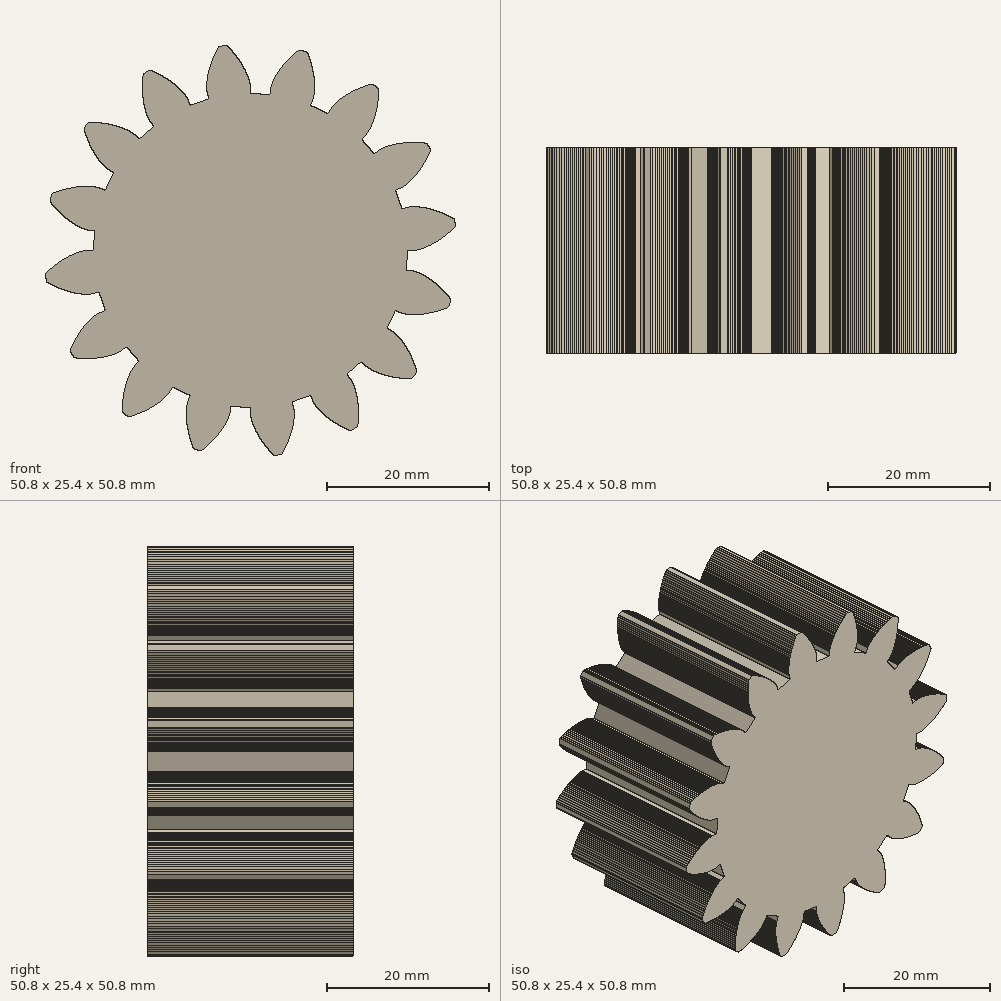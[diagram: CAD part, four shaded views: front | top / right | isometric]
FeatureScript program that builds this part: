
annotation { "Feature Type Name" : "Feature", "Feature Type Description" : "" }
export const myFeature = defineFeature(function(context is Context, id is Id, definition is map)
    precondition{}
    {
        {
            var Q0;
            Q0=qCreatedBy(makeId("Front.planeOp"),FACE);
            var sketch = newSketch(context, id + "F0", { "sketchPlane" : qUnion([Q0])});
            skLineSegment(sketch, "E0", {"start": v(19.47, 0) * mm, "end": v(20.26, 0) * mm});
            skLineSegment(sketch, "E1", {"start": v(20.26, 0) * mm, "end": v(20.27, 0) * mm});
            skLineSegment(sketch, "E2", {"start": v(20.27, 0) * mm, "end": v(20.3, 0) * mm});
            skLineSegment(sketch, "E3", {"start": v(20.3, 0) * mm, "end": v(20.33, 0) * mm});
            skLineSegment(sketch, "E4", {"start": v(20.33, 0) * mm, "end": v(20.37, 0) * mm});
            skLineSegment(sketch, "E5", {"start": v(20.37, 0) * mm, "end": v(20.42, 0.01) * mm});
            skLineSegment(sketch, "E6", {"start": v(20.42, 0.01) * mm, "end": v(20.48, 0.02) * mm});
            skLineSegment(sketch, "E7", {"start": v(20.48, 0.02) * mm, "end": v(20.55, 0.03) * mm});
            skLineSegment(sketch, "E8", {"start": v(20.55, 0.03) * mm, "end": v(20.63, 0.05) * mm});
            skLineSegment(sketch, "E9", {"start": v(20.63, 0.05) * mm, "end": v(20.72, 0.07) * mm});
            skLineSegment(sketch, "E10", {"start": v(20.72, 0.07) * mm, "end": v(20.81, 0.09) * mm});
            skLineSegment(sketch, "E11", {"start": v(20.81, 0.09) * mm, "end": v(20.92, 0.11) * mm});
            skLineSegment(sketch, "E12", {"start": v(20.92, 0.11) * mm, "end": v(21.03, 0.15) * mm});
            skLineSegment(sketch, "E13", {"start": v(21.03, 0.15) * mm, "end": v(21.15, 0.18) * mm});
            skLineSegment(sketch, "E14", {"start": v(21.15, 0.18) * mm, "end": v(21.29, 0.22) * mm});
            skLineSegment(sketch, "E15", {"start": v(21.29, 0.22) * mm, "end": v(21.43, 0.27) * mm});
            skLineSegment(sketch, "E16", {"start": v(21.43, 0.27) * mm, "end": v(21.57, 0.33) * mm});
            skLineSegment(sketch, "E17", {"start": v(21.57, 0.33) * mm, "end": v(21.73, 0.39) * mm});
            skLineSegment(sketch, "E18", {"start": v(21.73, 0.39) * mm, "end": v(21.9, 0.46) * mm});
            skLineSegment(sketch, "E19", {"start": v(21.9, 0.46) * mm, "end": v(22.06, 0.53) * mm});
            skLineSegment(sketch, "E20", {"start": v(22.06, 0.53) * mm, "end": v(22.24, 0.62) * mm});
            skLineSegment(sketch, "E21", {"start": v(22.24, 0.62) * mm, "end": v(22.42, 0.71) * mm});
            skLineSegment(sketch, "E22", {"start": v(22.42, 0.71) * mm, "end": v(22.61, 0.81) * mm});
            skLineSegment(sketch, "E23", {"start": v(22.61, 0.81) * mm, "end": v(22.8, 0.92) * mm});
            skLineSegment(sketch, "E24", {"start": v(22.8, 0.92) * mm, "end": v(23, 1.04) * mm});
            skLineSegment(sketch, "E25", {"start": v(23, 1.04) * mm, "end": v(23.22, 1.17) * mm});
            skLineSegment(sketch, "E26", {"start": v(23.22, 1.17) * mm, "end": v(23.43, 1.3) * mm});
            skLineSegment(sketch, "E27", {"start": v(23.43, 1.3) * mm, "end": v(23.65, 1.45) * mm});
            skLineSegment(sketch, "E28", {"start": v(23.65, 1.45) * mm, "end": v(23.87, 1.6) * mm});
            skLineSegment(sketch, "E29", {"start": v(23.87, 1.6) * mm, "end": v(24.1, 1.78) * mm});
            skLineSegment(sketch, "E30", {"start": v(24.1, 1.78) * mm, "end": v(24.33, 1.96) * mm});
            skLineSegment(sketch, "E31", {"start": v(24.33, 1.96) * mm, "end": v(24.56, 2.15) * mm});
            skLineSegment(sketch, "E32", {"start": v(24.56, 2.15) * mm, "end": v(24.8, 2.35) * mm});
            skLineSegment(sketch, "E33", {"start": v(24.8, 2.35) * mm, "end": v(25.04, 2.56) * mm});
            skLineSegment(sketch, "E34", {"start": v(25.04, 2.56) * mm, "end": v(25.28, 2.79) * mm});
            skLineSegment(sketch, "E35", {"start": v(25.28, 2.79) * mm, "end": v(25.4, 3.01) * mm});
            skLineSegment(sketch, "E36", {"start": v(25.4, 3.01) * mm, "end": v(25.3, 3.82) * mm});
            skLineSegment(sketch, "E37", {"start": v(25.3, 3.82) * mm, "end": v(25.12, 4) * mm});
            skLineSegment(sketch, "E38", {"start": v(25.12, 4) * mm, "end": v(24.82, 4.16) * mm});
            skLineSegment(sketch, "E39", {"start": v(24.82, 4.16) * mm, "end": v(24.54, 4.3) * mm});
            skLineSegment(sketch, "E40", {"start": v(24.54, 4.3) * mm, "end": v(24.25, 4.43) * mm});
            skLineSegment(sketch, "E41", {"start": v(24.25, 4.43) * mm, "end": v(23.98, 4.55) * mm});
            skLineSegment(sketch, "E42", {"start": v(23.98, 4.55) * mm, "end": v(23.7, 4.67) * mm});
            skLineSegment(sketch, "E43", {"start": v(23.7, 4.67) * mm, "end": v(23.44, 4.77) * mm});
            skLineSegment(sketch, "E44", {"start": v(23.44, 4.77) * mm, "end": v(23.19, 4.86) * mm});
            skLineSegment(sketch, "E45", {"start": v(23.19, 4.86) * mm, "end": v(22.94, 4.95) * mm});
            skLineSegment(sketch, "E46", {"start": v(22.94, 4.95) * mm, "end": v(22.7, 5.02) * mm});
            skLineSegment(sketch, "E47", {"start": v(22.7, 5.02) * mm, "end": v(22.46, 5.1) * mm});
            skLineSegment(sketch, "E48", {"start": v(22.46, 5.1) * mm, "end": v(22.24, 5.15) * mm});
            skLineSegment(sketch, "E49", {"start": v(22.24, 5.15) * mm, "end": v(22.02, 5.2) * mm});
            skLineSegment(sketch, "E50", {"start": v(22.02, 5.2) * mm, "end": v(21.8, 5.25) * mm});
            skLineSegment(sketch, "E51", {"start": v(21.8, 5.25) * mm, "end": v(21.6, 5.3) * mm});
            skLineSegment(sketch, "E52", {"start": v(21.6, 5.3) * mm, "end": v(21.41, 5.33) * mm});
            skLineSegment(sketch, "E53", {"start": v(21.41, 5.33) * mm, "end": v(21.23, 5.36) * mm});
            skLineSegment(sketch, "E54", {"start": v(21.23, 5.36) * mm, "end": v(21.06, 5.38) * mm});
            skLineSegment(sketch, "E55", {"start": v(21.06, 5.38) * mm, "end": v(20.89, 5.4) * mm});
            skLineSegment(sketch, "E56", {"start": v(20.89, 5.4) * mm, "end": v(20.73, 5.41) * mm});
            skLineSegment(sketch, "E57", {"start": v(20.73, 5.41) * mm, "end": v(20.59, 5.42) * mm});
            skLineSegment(sketch, "E58", {"start": v(20.59, 5.42) * mm, "end": v(20.45, 5.43) * mm});
            skLineSegment(sketch, "E59", {"start": v(20.45, 5.43) * mm, "end": v(20.32, 5.43) * mm});
            skLineSegment(sketch, "E60", {"start": v(20.32, 5.43) * mm, "end": v(20.2, 5.43) * mm});
            skLineSegment(sketch, "E61", {"start": v(20.2, 5.43) * mm, "end": v(20.1, 5.43) * mm});
            skLineSegment(sketch, "E62", {"start": v(20.1, 5.43) * mm, "end": v(20, 5.42) * mm});
            skLineSegment(sketch, "E63", {"start": v(20, 5.42) * mm, "end": v(19.9, 5.42) * mm});
            skLineSegment(sketch, "E64", {"start": v(19.9, 5.42) * mm, "end": v(19.82, 5.4) * mm});
            skLineSegment(sketch, "E65", {"start": v(19.82, 5.4) * mm, "end": v(19.75, 5.4) * mm});
            skLineSegment(sketch, "E66", {"start": v(19.75, 5.4) * mm, "end": v(19.7, 5.4) * mm});
            skLineSegment(sketch, "E67", {"start": v(19.7, 5.4) * mm, "end": v(19.64, 5.39) * mm});
            skLineSegment(sketch, "E68", {"start": v(19.64, 5.39) * mm, "end": v(19.6, 5.38) * mm});
            skLineSegment(sketch, "E69", {"start": v(19.6, 5.38) * mm, "end": v(19.57, 5.37) * mm});
            skLineSegment(sketch, "E70", {"start": v(19.57, 5.37) * mm, "end": v(19.55, 5.37) * mm});
            skLineSegment(sketch, "E71", {"start": v(19.55, 5.37) * mm, "end": v(19.54, 5.37) * mm});
            skLineSegment(sketch, "E72", {"start": v(19.54, 5.37) * mm, "end": v(18.77, 5.16) * mm});
            skLineSegment(sketch, "E73", {"start": v(18.77, 5.16) * mm, "end": v(17.99, 7.45) * mm});
            skLineSegment(sketch, "E74", {"start": v(17.99, 7.45) * mm, "end": v(18.72, 7.75) * mm});
            skLineSegment(sketch, "E75", {"start": v(18.72, 7.75) * mm, "end": v(18.73, 7.76) * mm});
            skLineSegment(sketch, "E76", {"start": v(18.73, 7.76) * mm, "end": v(18.75, 7.77) * mm});
            skLineSegment(sketch, "E77", {"start": v(18.75, 7.77) * mm, "end": v(18.78, 7.78) * mm});
            skLineSegment(sketch, "E78", {"start": v(18.78, 7.78) * mm, "end": v(18.82, 7.8) * mm});
            skLineSegment(sketch, "E79", {"start": v(18.82, 7.8) * mm, "end": v(18.86, 7.83) * mm});
            skLineSegment(sketch, "E80", {"start": v(18.86, 7.83) * mm, "end": v(18.91, 7.86) * mm});
            skLineSegment(sketch, "E81", {"start": v(18.91, 7.86) * mm, "end": v(18.97, 7.9) * mm});
            skLineSegment(sketch, "E82", {"start": v(18.97, 7.9) * mm, "end": v(19.04, 7.94) * mm});
            skLineSegment(sketch, "E83", {"start": v(19.04, 7.94) * mm, "end": v(19.11, 7.99) * mm});
            skLineSegment(sketch, "E84", {"start": v(19.11, 7.99) * mm, "end": v(19.2, 8.05) * mm});
            skLineSegment(sketch, "E85", {"start": v(19.2, 8.05) * mm, "end": v(19.28, 8.11) * mm});
            skLineSegment(sketch, "E86", {"start": v(19.28, 8.11) * mm, "end": v(19.38, 8.18) * mm});
            skLineSegment(sketch, "E87", {"start": v(19.38, 8.18) * mm, "end": v(19.47, 8.26) * mm});
            skLineSegment(sketch, "E88", {"start": v(19.47, 8.26) * mm, "end": v(19.58, 8.35) * mm});
            skLineSegment(sketch, "E89", {"start": v(19.58, 8.35) * mm, "end": v(19.7, 8.45) * mm});
            skLineSegment(sketch, "E90", {"start": v(19.7, 8.45) * mm, "end": v(19.8, 8.56) * mm});
            skLineSegment(sketch, "E91", {"start": v(19.8, 8.56) * mm, "end": v(19.93, 8.68) * mm});
            skLineSegment(sketch, "E92", {"start": v(19.93, 8.68) * mm, "end": v(20.05, 8.8) * mm});
            skLineSegment(sketch, "E93", {"start": v(20.05, 8.8) * mm, "end": v(20.18, 8.94) * mm});
            skLineSegment(sketch, "E94", {"start": v(20.18, 8.94) * mm, "end": v(20.3, 9.08) * mm});
            skLineSegment(sketch, "E95", {"start": v(20.3, 9.08) * mm, "end": v(20.44, 9.24) * mm});
            skLineSegment(sketch, "E96", {"start": v(20.44, 9.24) * mm, "end": v(20.58, 9.4) * mm});
            skLineSegment(sketch, "E97", {"start": v(20.58, 9.4) * mm, "end": v(20.72, 9.58) * mm});
            skLineSegment(sketch, "E98", {"start": v(20.72, 9.58) * mm, "end": v(20.86, 9.76) * mm});
            skLineSegment(sketch, "E99", {"start": v(20.86, 9.76) * mm, "end": v(21, 9.96) * mm});
            skLineSegment(sketch, "E100", {"start": v(21, 9.96) * mm, "end": v(21.15, 10.17) * mm});
            skLineSegment(sketch, "E101", {"start": v(21.15, 10.17) * mm, "end": v(21.3, 10.4) * mm});
            skLineSegment(sketch, "E102", {"start": v(21.3, 10.4) * mm, "end": v(21.44, 10.62) * mm});
            skLineSegment(sketch, "E103", {"start": v(21.44, 10.62) * mm, "end": v(21.58, 10.86) * mm});
            skLineSegment(sketch, "E104", {"start": v(21.58, 10.86) * mm, "end": v(21.73, 11.12) * mm});
            skLineSegment(sketch, "E105", {"start": v(21.73, 11.12) * mm, "end": v(21.87, 11.38) * mm});
            skLineSegment(sketch, "E106", {"start": v(21.87, 11.38) * mm, "end": v(22.01, 11.66) * mm});
            skLineSegment(sketch, "E107", {"start": v(22.01, 11.66) * mm, "end": v(22.15, 11.95) * mm});
            skLineSegment(sketch, "E108", {"start": v(22.15, 11.95) * mm, "end": v(22.29, 12.25) * mm});
            skLineSegment(sketch, "E109", {"start": v(22.29, 12.25) * mm, "end": v(22.31, 12.5) * mm});
            skLineSegment(sketch, "E110", {"start": v(22.31, 12.5) * mm, "end": v(21.9, 13.21) * mm});
            skLineSegment(sketch, "E111", {"start": v(21.9, 13.21) * mm, "end": v(21.67, 13.31) * mm});
            skLineSegment(sketch, "E112", {"start": v(21.67, 13.31) * mm, "end": v(21.34, 13.34) * mm});
            skLineSegment(sketch, "E113", {"start": v(21.34, 13.34) * mm, "end": v(21.02, 13.36) * mm});
            skLineSegment(sketch, "E114", {"start": v(21.02, 13.36) * mm, "end": v(20.71, 13.38) * mm});
            skLineSegment(sketch, "E115", {"start": v(20.71, 13.38) * mm, "end": v(20.4, 13.38) * mm});
            skLineSegment(sketch, "E116", {"start": v(20.4, 13.38) * mm, "end": v(20.12, 13.38) * mm});
            skLineSegment(sketch, "E117", {"start": v(20.12, 13.38) * mm, "end": v(19.83, 13.38) * mm});
            skLineSegment(sketch, "E118", {"start": v(19.83, 13.38) * mm, "end": v(19.56, 13.37) * mm});
            skLineSegment(sketch, "E119", {"start": v(19.56, 13.37) * mm, "end": v(19.3, 13.35) * mm});
            skLineSegment(sketch, "E120", {"start": v(19.3, 13.35) * mm, "end": v(19.05, 13.33) * mm});
            skLineSegment(sketch, "E121", {"start": v(19.05, 13.33) * mm, "end": v(18.8, 13.3) * mm});
            skLineSegment(sketch, "E122", {"start": v(18.8, 13.3) * mm, "end": v(18.57, 13.27) * mm});
            skLineSegment(sketch, "E123", {"start": v(18.57, 13.27) * mm, "end": v(18.35, 13.24) * mm});
            skLineSegment(sketch, "E124", {"start": v(18.35, 13.24) * mm, "end": v(18.14, 13.2) * mm});
            skLineSegment(sketch, "E125", {"start": v(18.14, 13.2) * mm, "end": v(17.94, 13.16) * mm});
            skLineSegment(sketch, "E126", {"start": v(17.94, 13.16) * mm, "end": v(17.75, 13.12) * mm});
            skLineSegment(sketch, "E127", {"start": v(17.75, 13.12) * mm, "end": v(17.56, 13.07) * mm});
            skLineSegment(sketch, "E128", {"start": v(17.56, 13.07) * mm, "end": v(17.4, 13.03) * mm});
            skLineSegment(sketch, "E129", {"start": v(17.4, 13.03) * mm, "end": v(17.23, 12.98) * mm});
            skLineSegment(sketch, "E130", {"start": v(17.23, 12.98) * mm, "end": v(17.08, 12.93) * mm});
            skLineSegment(sketch, "E131", {"start": v(17.08, 12.93) * mm, "end": v(16.94, 12.89) * mm});
            skLineSegment(sketch, "E132", {"start": v(16.94, 12.89) * mm, "end": v(16.82, 12.84) * mm});
            skLineSegment(sketch, "E133", {"start": v(16.82, 12.84) * mm, "end": v(16.7, 12.8) * mm});
            skLineSegment(sketch, "E134", {"start": v(16.7, 12.8) * mm, "end": v(16.59, 12.75) * mm});
            skLineSegment(sketch, "E135", {"start": v(16.59, 12.75) * mm, "end": v(16.49, 12.7) * mm});
            skLineSegment(sketch, "E136", {"start": v(16.49, 12.7) * mm, "end": v(16.4, 12.66) * mm});
            skLineSegment(sketch, "E137", {"start": v(16.4, 12.66) * mm, "end": v(16.32, 12.62) * mm});
            skLineSegment(sketch, "E138", {"start": v(16.32, 12.62) * mm, "end": v(16.24, 12.58) * mm});
            skLineSegment(sketch, "E139", {"start": v(16.24, 12.58) * mm, "end": v(16.18, 12.55) * mm});
            skLineSegment(sketch, "E140", {"start": v(16.18, 12.55) * mm, "end": v(16.13, 12.52) * mm});
            skLineSegment(sketch, "E141", {"start": v(16.13, 12.52) * mm, "end": v(16.09, 12.5) * mm});
            skLineSegment(sketch, "E142", {"start": v(16.09, 12.5) * mm, "end": v(16.05, 12.47) * mm});
            skLineSegment(sketch, "E143", {"start": v(16.05, 12.47) * mm, "end": v(16.03, 12.45) * mm});
            skLineSegment(sketch, "E144", {"start": v(16.03, 12.45) * mm, "end": v(16, 12.44) * mm});
            skLineSegment(sketch, "E145", {"start": v(16, 12.44) * mm, "end": v(16, 12.43) * mm});
            skLineSegment(sketch, "E146", {"start": v(16, 12.43) * mm, "end": v(15.37, 11.95) * mm});
            skLineSegment(sketch, "E147", {"start": v(15.37, 11.95) * mm, "end": v(13.77, 13.77) * mm});
            skLineSegment(sketch, "E148", {"start": v(13.77, 13.77) * mm, "end": v(14.33, 14.33) * mm});
            skLineSegment(sketch, "E149", {"start": v(14.33, 14.33) * mm, "end": v(14.34, 14.34) * mm});
            skLineSegment(sketch, "E150", {"start": v(14.34, 14.34) * mm, "end": v(14.35, 14.35) * mm});
            skLineSegment(sketch, "E151", {"start": v(14.35, 14.35) * mm, "end": v(14.37, 14.38) * mm});
            skLineSegment(sketch, "E152", {"start": v(14.37, 14.38) * mm, "end": v(14.4, 14.4) * mm});
            skLineSegment(sketch, "E153", {"start": v(14.4, 14.4) * mm, "end": v(14.43, 14.45) * mm});
            skLineSegment(sketch, "E154", {"start": v(14.43, 14.45) * mm, "end": v(14.47, 14.5) * mm});
            skLineSegment(sketch, "E155", {"start": v(14.47, 14.5) * mm, "end": v(14.5, 14.55) * mm});
            skLineSegment(sketch, "E156", {"start": v(14.5, 14.55) * mm, "end": v(14.55, 14.62) * mm});
            skLineSegment(sketch, "E157", {"start": v(14.55, 14.62) * mm, "end": v(14.6, 14.7) * mm});
            skLineSegment(sketch, "E158", {"start": v(14.6, 14.7) * mm, "end": v(14.65, 14.78) * mm});
            skLineSegment(sketch, "E159", {"start": v(14.65, 14.78) * mm, "end": v(14.71, 14.87) * mm});
            skLineSegment(sketch, "E160", {"start": v(14.71, 14.87) * mm, "end": v(14.77, 14.98) * mm});
            skLineSegment(sketch, "E161", {"start": v(14.77, 14.98) * mm, "end": v(14.83, 15.09) * mm});
            skLineSegment(sketch, "E162", {"start": v(14.83, 15.09) * mm, "end": v(14.9, 15.21) * mm});
            skLineSegment(sketch, "E163", {"start": v(14.9, 15.21) * mm, "end": v(14.96, 15.34) * mm});
            skLineSegment(sketch, "E164", {"start": v(14.96, 15.34) * mm, "end": v(15.02, 15.49) * mm});
            skLineSegment(sketch, "E165", {"start": v(15.02, 15.49) * mm, "end": v(15.09, 15.64) * mm});
            skLineSegment(sketch, "E166", {"start": v(15.09, 15.64) * mm, "end": v(15.15, 15.8) * mm});
            skLineSegment(sketch, "E167", {"start": v(15.15, 15.8) * mm, "end": v(15.22, 15.98) * mm});
            skLineSegment(sketch, "E168", {"start": v(15.22, 15.98) * mm, "end": v(15.29, 16.16) * mm});
            skLineSegment(sketch, "E169", {"start": v(15.29, 16.16) * mm, "end": v(15.35, 16.36) * mm});
            skLineSegment(sketch, "E170", {"start": v(15.35, 16.36) * mm, "end": v(15.42, 16.56) * mm});
            skLineSegment(sketch, "E171", {"start": v(15.42, 16.56) * mm, "end": v(15.48, 16.78) * mm});
            skLineSegment(sketch, "E172", {"start": v(15.48, 16.78) * mm, "end": v(15.54, 17) * mm});
            skLineSegment(sketch, "E173", {"start": v(15.54, 17) * mm, "end": v(15.6, 17.24) * mm});
            skLineSegment(sketch, "E174", {"start": v(15.6, 17.24) * mm, "end": v(15.65, 17.49) * mm});
            skLineSegment(sketch, "E175", {"start": v(15.65, 17.49) * mm, "end": v(15.7, 17.75) * mm});
            skLineSegment(sketch, "E176", {"start": v(15.7, 17.75) * mm, "end": v(15.74, 18.02) * mm});
            skLineSegment(sketch, "E177", {"start": v(15.74, 18.02) * mm, "end": v(15.78, 18.3) * mm});
            skLineSegment(sketch, "E178", {"start": v(15.78, 18.3) * mm, "end": v(15.82, 18.59) * mm});
            skLineSegment(sketch, "E179", {"start": v(15.82, 18.59) * mm, "end": v(15.85, 18.89) * mm});
            skLineSegment(sketch, "E180", {"start": v(15.85, 18.89) * mm, "end": v(15.87, 19.2) * mm});
            skLineSegment(sketch, "E181", {"start": v(15.87, 19.2) * mm, "end": v(15.9, 19.52) * mm});
            skLineSegment(sketch, "E182", {"start": v(15.9, 19.52) * mm, "end": v(15.9, 19.85) * mm});
            skLineSegment(sketch, "E183", {"start": v(15.9, 19.85) * mm, "end": v(15.83, 20.09) * mm});
            skLineSegment(sketch, "E184", {"start": v(15.83, 20.09) * mm, "end": v(15.18, 20.59) * mm});
            skLineSegment(sketch, "E185", {"start": v(15.18, 20.59) * mm, "end": v(14.93, 20.6) * mm});
            skLineSegment(sketch, "E186", {"start": v(14.93, 20.6) * mm, "end": v(14.61, 20.5) * mm});
            skLineSegment(sketch, "E187", {"start": v(14.61, 20.5) * mm, "end": v(14.3, 20.4) * mm});
            skLineSegment(sketch, "E188", {"start": v(14.3, 20.4) * mm, "end": v(14.02, 20.28) * mm});
            skLineSegment(sketch, "E189", {"start": v(14.02, 20.28) * mm, "end": v(13.73, 20.18) * mm});
            skLineSegment(sketch, "E190", {"start": v(13.73, 20.18) * mm, "end": v(13.46, 20.06) * mm});
            skLineSegment(sketch, "E191", {"start": v(13.46, 20.06) * mm, "end": v(13.2, 19.95) * mm});
            skLineSegment(sketch, "E192", {"start": v(13.2, 19.95) * mm, "end": v(12.96, 19.83) * mm});
            skLineSegment(sketch, "E193", {"start": v(12.96, 19.83) * mm, "end": v(12.72, 19.72) * mm});
            skLineSegment(sketch, "E194", {"start": v(12.72, 19.72) * mm, "end": v(12.5, 19.6) * mm});
            skLineSegment(sketch, "E195", {"start": v(12.5, 19.6) * mm, "end": v(12.28, 19.48) * mm});
            skLineSegment(sketch, "E196", {"start": v(12.28, 19.48) * mm, "end": v(12.08, 19.37) * mm});
            skLineSegment(sketch, "E197", {"start": v(12.08, 19.37) * mm, "end": v(11.89, 19.25) * mm});
            skLineSegment(sketch, "E198", {"start": v(11.89, 19.25) * mm, "end": v(11.7, 19.14) * mm});
            skLineSegment(sketch, "E199", {"start": v(11.7, 19.14) * mm, "end": v(11.54, 19.02) * mm});
            skLineSegment(sketch, "E200", {"start": v(11.54, 19.02) * mm, "end": v(11.38, 18.9) * mm});
            skLineSegment(sketch, "E201", {"start": v(11.38, 18.9) * mm, "end": v(11.23, 18.8) * mm});
            skLineSegment(sketch, "E202", {"start": v(11.23, 18.8) * mm, "end": v(11.09, 18.7) * mm});
            skLineSegment(sketch, "E203", {"start": v(11.09, 18.7) * mm, "end": v(10.96, 18.59) * mm});
            skLineSegment(sketch, "E204", {"start": v(10.96, 18.59) * mm, "end": v(10.83, 18.49) * mm});
            skLineSegment(sketch, "E205", {"start": v(10.83, 18.49) * mm, "end": v(10.72, 18.39) * mm});
            skLineSegment(sketch, "E206", {"start": v(10.72, 18.39) * mm, "end": v(10.62, 18.3) * mm});
            skLineSegment(sketch, "E207", {"start": v(10.62, 18.3) * mm, "end": v(10.53, 18.2) * mm});
            skLineSegment(sketch, "E208", {"start": v(10.53, 18.2) * mm, "end": v(10.45, 18.12) * mm});
            skLineSegment(sketch, "E209", {"start": v(10.45, 18.12) * mm, "end": v(10.37, 18.04) * mm});
            skLineSegment(sketch, "E210", {"start": v(10.37, 18.04) * mm, "end": v(10.3, 17.97) * mm});
            skLineSegment(sketch, "E211", {"start": v(10.3, 17.97) * mm, "end": v(10.24, 17.9) * mm});
            skLineSegment(sketch, "E212", {"start": v(10.24, 17.9) * mm, "end": v(10.2, 17.84) * mm});
            skLineSegment(sketch, "E213", {"start": v(10.2, 17.84) * mm, "end": v(10.15, 17.79) * mm});
            skLineSegment(sketch, "E214", {"start": v(10.15, 17.79) * mm, "end": v(10.11, 17.74) * mm});
            skLineSegment(sketch, "E215", {"start": v(10.11, 17.74) * mm, "end": v(10.08, 17.7) * mm});
            skLineSegment(sketch, "E216", {"start": v(10.08, 17.7) * mm, "end": v(10.06, 17.67) * mm});
            skLineSegment(sketch, "E217", {"start": v(10.06, 17.67) * mm, "end": v(10.04, 17.64) * mm});
            skLineSegment(sketch, "E218", {"start": v(10.04, 17.64) * mm, "end": v(10.03, 17.62) * mm});
            skLineSegment(sketch, "E219", {"start": v(10.03, 17.62) * mm, "end": v(10.02, 17.6) * mm});
            skLineSegment(sketch, "E220", {"start": v(10.02, 17.6) * mm, "end": v(9.63, 16.92) * mm});
            skLineSegment(sketch, "E221", {"start": v(9.63, 16.92) * mm, "end": v(7.45, 17.99) * mm});
            skLineSegment(sketch, "E222", {"start": v(7.45, 17.99) * mm, "end": v(7.75, 18.72) * mm});
            skLineSegment(sketch, "E223", {"start": v(7.75, 18.72) * mm, "end": v(7.76, 18.73) * mm});
            skLineSegment(sketch, "E224", {"start": v(7.76, 18.73) * mm, "end": v(7.77, 18.75) * mm});
            skLineSegment(sketch, "E225", {"start": v(7.77, 18.75) * mm, "end": v(7.78, 18.78) * mm});
            skLineSegment(sketch, "E226", {"start": v(7.78, 18.78) * mm, "end": v(7.79, 18.82) * mm});
            skLineSegment(sketch, "E227", {"start": v(7.79, 18.82) * mm, "end": v(7.8, 18.87) * mm});
            skLineSegment(sketch, "E228", {"start": v(7.8, 18.87) * mm, "end": v(7.82, 18.93) * mm});
            skLineSegment(sketch, "E229", {"start": v(7.82, 18.93) * mm, "end": v(7.83, 19) * mm});
            skLineSegment(sketch, "E230", {"start": v(7.83, 19) * mm, "end": v(7.85, 19.08) * mm});
            skLineSegment(sketch, "E231", {"start": v(7.85, 19.08) * mm, "end": v(7.87, 19.16) * mm});
            skLineSegment(sketch, "E232", {"start": v(7.87, 19.16) * mm, "end": v(7.88, 19.26) * mm});
            skLineSegment(sketch, "E233", {"start": v(7.88, 19.26) * mm, "end": v(7.9, 19.37) * mm});
            skLineSegment(sketch, "E234", {"start": v(7.9, 19.37) * mm, "end": v(7.91, 19.49) * mm});
            skLineSegment(sketch, "E235", {"start": v(7.91, 19.49) * mm, "end": v(7.93, 19.61) * mm});
            skLineSegment(sketch, "E236", {"start": v(7.93, 19.61) * mm, "end": v(7.94, 19.75) * mm});
            skLineSegment(sketch, "E237", {"start": v(7.94, 19.75) * mm, "end": v(7.95, 19.9) * mm});
            skLineSegment(sketch, "E238", {"start": v(7.95, 19.9) * mm, "end": v(7.95, 20.06) * mm});
            skLineSegment(sketch, "E239", {"start": v(7.95, 20.06) * mm, "end": v(7.96, 20.22) * mm});
            skLineSegment(sketch, "E240", {"start": v(7.96, 20.22) * mm, "end": v(7.95, 20.4) * mm});
            skLineSegment(sketch, "E241", {"start": v(7.95, 20.4) * mm, "end": v(7.95, 20.59) * mm});
            skLineSegment(sketch, "E242", {"start": v(7.95, 20.59) * mm, "end": v(7.94, 20.78) * mm});
            skLineSegment(sketch, "E243", {"start": v(7.94, 20.78) * mm, "end": v(7.92, 20.99) * mm});
            skLineSegment(sketch, "E244", {"start": v(7.92, 20.99) * mm, "end": v(7.9, 21.2) * mm});
            skLineSegment(sketch, "E245", {"start": v(7.9, 21.2) * mm, "end": v(7.88, 21.42) * mm});
            skLineSegment(sketch, "E246", {"start": v(7.88, 21.42) * mm, "end": v(7.85, 21.66) * mm});
            skLineSegment(sketch, "E247", {"start": v(7.85, 21.66) * mm, "end": v(7.8, 21.9) * mm});
            skLineSegment(sketch, "E248", {"start": v(7.8, 21.9) * mm, "end": v(7.76, 22.15) * mm});
            skLineSegment(sketch, "E249", {"start": v(7.76, 22.15) * mm, "end": v(7.7, 22.4) * mm});
            skLineSegment(sketch, "E250", {"start": v(7.7, 22.4) * mm, "end": v(7.65, 22.67) * mm});
            skLineSegment(sketch, "E251", {"start": v(7.65, 22.67) * mm, "end": v(7.58, 22.94) * mm});
            skLineSegment(sketch, "E252", {"start": v(7.58, 22.94) * mm, "end": v(7.5, 23.22) * mm});
            skLineSegment(sketch, "E253", {"start": v(7.5, 23.22) * mm, "end": v(7.41, 23.51) * mm});
            skLineSegment(sketch, "E254", {"start": v(7.41, 23.51) * mm, "end": v(7.32, 23.81) * mm});
            skLineSegment(sketch, "E255", {"start": v(7.32, 23.81) * mm, "end": v(7.21, 24.11) * mm});
            skLineSegment(sketch, "E256", {"start": v(7.21, 24.11) * mm, "end": v(7.1, 24.42) * mm});
            skLineSegment(sketch, "E257", {"start": v(7.1, 24.42) * mm, "end": v(6.94, 24.62) * mm});
            skLineSegment(sketch, "E258", {"start": v(6.94, 24.62) * mm, "end": v(6.15, 24.83) * mm});
            skLineSegment(sketch, "E259", {"start": v(6.15, 24.83) * mm, "end": v(5.91, 24.74) * mm});
            skLineSegment(sketch, "E260", {"start": v(5.91, 24.74) * mm, "end": v(5.66, 24.53) * mm});
            skLineSegment(sketch, "E261", {"start": v(5.66, 24.53) * mm, "end": v(5.42, 24.31) * mm});
            skLineSegment(sketch, "E262", {"start": v(5.42, 24.31) * mm, "end": v(5.19, 24.1) * mm});
            skLineSegment(sketch, "E263", {"start": v(5.19, 24.1) * mm, "end": v(4.97, 23.9) * mm});
            skLineSegment(sketch, "E264", {"start": v(4.97, 23.9) * mm, "end": v(4.76, 23.69) * mm});
            skLineSegment(sketch, "E265", {"start": v(4.76, 23.69) * mm, "end": v(4.57, 23.48) * mm});
            skLineSegment(sketch, "E266", {"start": v(4.57, 23.48) * mm, "end": v(4.38, 23.28) * mm});
            skLineSegment(sketch, "E267", {"start": v(4.38, 23.28) * mm, "end": v(4.2, 23.09) * mm});
            skLineSegment(sketch, "E268", {"start": v(4.2, 23.09) * mm, "end": v(4.04, 22.9) * mm});
            skLineSegment(sketch, "E269", {"start": v(4.04, 22.9) * mm, "end": v(3.9, 22.7) * mm});
            skLineSegment(sketch, "E270", {"start": v(3.9, 22.7) * mm, "end": v(3.75, 22.52) * mm});
            skLineSegment(sketch, "E271", {"start": v(3.75, 22.52) * mm, "end": v(3.62, 22.33) * mm});
            skLineSegment(sketch, "E272", {"start": v(3.62, 22.33) * mm, "end": v(3.5, 22.16) * mm});
            skLineSegment(sketch, "E273", {"start": v(3.5, 22.16) * mm, "end": v(3.38, 21.99) * mm});
            skLineSegment(sketch, "E274", {"start": v(3.38, 21.99) * mm, "end": v(3.27, 21.82) * mm});
            skLineSegment(sketch, "E275", {"start": v(3.27, 21.82) * mm, "end": v(3.18, 21.66) * mm});
            skLineSegment(sketch, "E276", {"start": v(3.18, 21.66) * mm, "end": v(3.09, 21.51) * mm});
            skLineSegment(sketch, "E277", {"start": v(3.09, 21.51) * mm, "end": v(3, 21.36) * mm});
            skLineSegment(sketch, "E278", {"start": v(3, 21.36) * mm, "end": v(2.94, 21.23) * mm});
            skLineSegment(sketch, "E279", {"start": v(2.94, 21.23) * mm, "end": v(2.87, 21.1) * mm});
            skLineSegment(sketch, "E280", {"start": v(2.87, 21.1) * mm, "end": v(2.81, 20.97) * mm});
            skLineSegment(sketch, "E281", {"start": v(2.81, 20.97) * mm, "end": v(2.76, 20.85) * mm});
            skLineSegment(sketch, "E282", {"start": v(2.76, 20.85) * mm, "end": v(2.71, 20.74) * mm});
            skLineSegment(sketch, "E283", {"start": v(2.71, 20.74) * mm, "end": v(2.67, 20.64) * mm});
            skLineSegment(sketch, "E284", {"start": v(2.67, 20.64) * mm, "end": v(2.64, 20.55) * mm});
            skLineSegment(sketch, "E285", {"start": v(2.64, 20.55) * mm, "end": v(2.61, 20.46) * mm});
            skLineSegment(sketch, "E286", {"start": v(2.61, 20.46) * mm, "end": v(2.59, 20.39) * mm});
            skLineSegment(sketch, "E287", {"start": v(2.59, 20.39) * mm, "end": v(2.57, 20.32) * mm});
            skLineSegment(sketch, "E288", {"start": v(2.57, 20.32) * mm, "end": v(2.55, 20.26) * mm});
            skLineSegment(sketch, "E289", {"start": v(2.55, 20.26) * mm, "end": v(2.54, 20.2) * mm});
            skLineSegment(sketch, "E290", {"start": v(2.54, 20.2) * mm, "end": v(2.53, 20.17) * mm});
            skLineSegment(sketch, "E291", {"start": v(2.53, 20.17) * mm, "end": v(2.53, 20.14) * mm});
            skLineSegment(sketch, "E292", {"start": v(2.53, 20.14) * mm, "end": v(2.52, 20.12) * mm});
            skLineSegment(sketch, "E293", {"start": v(2.52, 20.12) * mm, "end": v(2.52, 20.1) * mm});
            skLineSegment(sketch, "E294", {"start": v(2.52, 20.1) * mm, "end": v(2.42, 19.32) * mm});
            skLineSegment(sketch, "E295", {"start": v(2.42, 19.32) * mm, "end": v(0, 19.47) * mm});
            skLineSegment(sketch, "E296", {"start": v(0, 19.47) * mm, "end": v(0, 20.26) * mm});
            skLineSegment(sketch, "E297", {"start": v(0, 20.26) * mm, "end": v(0, 20.27) * mm});
            skLineSegment(sketch, "E298", {"start": v(0, 20.27) * mm, "end": v(0, 20.3) * mm});
            skLineSegment(sketch, "E299", {"start": v(0, 20.3) * mm, "end": v(0, 20.33) * mm});
            skLineSegment(sketch, "E300", {"start": v(0, 20.33) * mm, "end": v(0, 20.37) * mm});
            skLineSegment(sketch, "E301", {"start": v(0, 20.37) * mm, "end": v(-0.01, 20.42) * mm});
            skLineSegment(sketch, "E302", {"start": v(-0.01, 20.42) * mm, "end": v(-0.02, 20.48) * mm});
            skLineSegment(sketch, "E303", {"start": v(-0.02, 20.48) * mm, "end": v(-0.03, 20.55) * mm});
            skLineSegment(sketch, "E304", {"start": v(-0.03, 20.55) * mm, "end": v(-0.05, 20.63) * mm});
            skLineSegment(sketch, "E305", {"start": v(-0.05, 20.63) * mm, "end": v(-0.07, 20.72) * mm});
            skLineSegment(sketch, "E306", {"start": v(-0.07, 20.72) * mm, "end": v(-0.09, 20.81) * mm});
            skLineSegment(sketch, "E307", {"start": v(-0.09, 20.81) * mm, "end": v(-0.11, 20.92) * mm});
            skLineSegment(sketch, "E308", {"start": v(-0.11, 20.92) * mm, "end": v(-0.15, 21.03) * mm});
            skLineSegment(sketch, "E309", {"start": v(-0.15, 21.03) * mm, "end": v(-0.18, 21.15) * mm});
            skLineSegment(sketch, "E310", {"start": v(-0.18, 21.15) * mm, "end": v(-0.22, 21.29) * mm});
            skLineSegment(sketch, "E311", {"start": v(-0.22, 21.29) * mm, "end": v(-0.27, 21.43) * mm});
            skLineSegment(sketch, "E312", {"start": v(-0.27, 21.43) * mm, "end": v(-0.33, 21.57) * mm});
            skLineSegment(sketch, "E313", {"start": v(-0.33, 21.57) * mm, "end": v(-0.39, 21.73) * mm});
            skLineSegment(sketch, "E314", {"start": v(-0.39, 21.73) * mm, "end": v(-0.46, 21.9) * mm});
            skLineSegment(sketch, "E315", {"start": v(-0.46, 21.9) * mm, "end": v(-0.53, 22.06) * mm});
            skLineSegment(sketch, "E316", {"start": v(-0.53, 22.06) * mm, "end": v(-0.62, 22.24) * mm});
            skLineSegment(sketch, "E317", {"start": v(-0.62, 22.24) * mm, "end": v(-0.7, 22.42) * mm});
            skLineSegment(sketch, "E318", {"start": v(-0.7, 22.42) * mm, "end": v(-0.81, 22.61) * mm});
            skLineSegment(sketch, "E319", {"start": v(-0.81, 22.61) * mm, "end": v(-0.92, 22.8) * mm});
            skLineSegment(sketch, "E320", {"start": v(-0.92, 22.8) * mm, "end": v(-1.04, 23) * mm});
            skLineSegment(sketch, "E321", {"start": v(-1.04, 23) * mm, "end": v(-1.17, 23.22) * mm});
            skLineSegment(sketch, "E322", {"start": v(-1.17, 23.22) * mm, "end": v(-1.3, 23.43) * mm});
            skLineSegment(sketch, "E323", {"start": v(-1.3, 23.43) * mm, "end": v(-1.45, 23.65) * mm});
            skLineSegment(sketch, "E324", {"start": v(-1.45, 23.65) * mm, "end": v(-1.6, 23.87) * mm});
            skLineSegment(sketch, "E325", {"start": v(-1.6, 23.87) * mm, "end": v(-1.78, 24.1) * mm});
            skLineSegment(sketch, "E326", {"start": v(-1.78, 24.1) * mm, "end": v(-1.96, 24.33) * mm});
            skLineSegment(sketch, "E327", {"start": v(-1.96, 24.33) * mm, "end": v(-2.15, 24.56) * mm});
            skLineSegment(sketch, "E328", {"start": v(-2.15, 24.56) * mm, "end": v(-2.35, 24.8) * mm});
            skLineSegment(sketch, "E329", {"start": v(-2.35, 24.8) * mm, "end": v(-2.56, 25.04) * mm});
            skLineSegment(sketch, "E330", {"start": v(-2.56, 25.04) * mm, "end": v(-2.79, 25.28) * mm});
            skLineSegment(sketch, "E331", {"start": v(-2.79, 25.28) * mm, "end": v(-3.01, 25.4) * mm});
            skLineSegment(sketch, "E332", {"start": v(-3.01, 25.4) * mm, "end": v(-3.82, 25.3) * mm});
            skLineSegment(sketch, "E333", {"start": v(-3.82, 25.3) * mm, "end": v(-4, 25.12) * mm});
            skLineSegment(sketch, "E334", {"start": v(-4, 25.12) * mm, "end": v(-4.16, 24.82) * mm});
            skLineSegment(sketch, "E335", {"start": v(-4.16, 24.82) * mm, "end": v(-4.3, 24.54) * mm});
            skLineSegment(sketch, "E336", {"start": v(-4.3, 24.54) * mm, "end": v(-4.43, 24.25) * mm});
            skLineSegment(sketch, "E337", {"start": v(-4.43, 24.25) * mm, "end": v(-4.55, 23.98) * mm});
            skLineSegment(sketch, "E338", {"start": v(-4.55, 23.98) * mm, "end": v(-4.67, 23.7) * mm});
            skLineSegment(sketch, "E339", {"start": v(-4.67, 23.7) * mm, "end": v(-4.77, 23.44) * mm});
            skLineSegment(sketch, "E340", {"start": v(-4.77, 23.44) * mm, "end": v(-4.86, 23.19) * mm});
            skLineSegment(sketch, "E341", {"start": v(-4.86, 23.19) * mm, "end": v(-4.95, 22.94) * mm});
            skLineSegment(sketch, "E342", {"start": v(-4.95, 22.94) * mm, "end": v(-5.02, 22.7) * mm});
            skLineSegment(sketch, "E343", {"start": v(-5.02, 22.7) * mm, "end": v(-5.1, 22.46) * mm});
            skLineSegment(sketch, "E344", {"start": v(-5.1, 22.46) * mm, "end": v(-5.15, 22.24) * mm});
            skLineSegment(sketch, "E345", {"start": v(-5.15, 22.24) * mm, "end": v(-5.2, 22.02) * mm});
            skLineSegment(sketch, "E346", {"start": v(-5.2, 22.02) * mm, "end": v(-5.25, 21.8) * mm});
            skLineSegment(sketch, "E347", {"start": v(-5.25, 21.8) * mm, "end": v(-5.3, 21.6) * mm});
            skLineSegment(sketch, "E348", {"start": v(-5.3, 21.6) * mm, "end": v(-5.33, 21.41) * mm});
            skLineSegment(sketch, "E349", {"start": v(-5.33, 21.41) * mm, "end": v(-5.36, 21.23) * mm});
            skLineSegment(sketch, "E350", {"start": v(-5.36, 21.23) * mm, "end": v(-5.38, 21.06) * mm});
            skLineSegment(sketch, "E351", {"start": v(-5.38, 21.06) * mm, "end": v(-5.4, 20.89) * mm});
            skLineSegment(sketch, "E352", {"start": v(-5.4, 20.89) * mm, "end": v(-5.41, 20.73) * mm});
            skLineSegment(sketch, "E353", {"start": v(-5.41, 20.73) * mm, "end": v(-5.42, 20.59) * mm});
            skLineSegment(sketch, "E354", {"start": v(-5.42, 20.59) * mm, "end": v(-5.43, 20.45) * mm});
            skLineSegment(sketch, "E355", {"start": v(-5.43, 20.45) * mm, "end": v(-5.43, 20.32) * mm});
            skLineSegment(sketch, "E356", {"start": v(-5.43, 20.32) * mm, "end": v(-5.43, 20.2) * mm});
            skLineSegment(sketch, "E357", {"start": v(-5.43, 20.2) * mm, "end": v(-5.43, 20.1) * mm});
            skLineSegment(sketch, "E358", {"start": v(-5.43, 20.1) * mm, "end": v(-5.42, 20) * mm});
            skLineSegment(sketch, "E359", {"start": v(-5.42, 20) * mm, "end": v(-5.42, 19.9) * mm});
            skLineSegment(sketch, "E360", {"start": v(-5.42, 19.9) * mm, "end": v(-5.4, 19.82) * mm});
            skLineSegment(sketch, "E361", {"start": v(-5.4, 19.82) * mm, "end": v(-5.4, 19.75) * mm});
            skLineSegment(sketch, "E362", {"start": v(-5.4, 19.75) * mm, "end": v(-5.4, 19.7) * mm});
            skLineSegment(sketch, "E363", {"start": v(-5.4, 19.7) * mm, "end": v(-5.39, 19.64) * mm});
            skLineSegment(sketch, "E364", {"start": v(-5.39, 19.64) * mm, "end": v(-5.38, 19.6) * mm});
            skLineSegment(sketch, "E365", {"start": v(-5.38, 19.6) * mm, "end": v(-5.37, 19.57) * mm});
            skLineSegment(sketch, "E366", {"start": v(-5.37, 19.57) * mm, "end": v(-5.37, 19.55) * mm});
            skLineSegment(sketch, "E367", {"start": v(-5.37, 19.55) * mm, "end": v(-5.37, 19.54) * mm});
            skLineSegment(sketch, "E368", {"start": v(-5.37, 19.54) * mm, "end": v(-5.16, 18.77) * mm});
            skLineSegment(sketch, "E369", {"start": v(-5.16, 18.77) * mm, "end": v(-7.45, 17.99) * mm});
            skLineSegment(sketch, "E370", {"start": v(-7.45, 17.99) * mm, "end": v(-7.75, 18.72) * mm});
            skLineSegment(sketch, "E371", {"start": v(-7.75, 18.72) * mm, "end": v(-7.76, 18.73) * mm});
            skLineSegment(sketch, "E372", {"start": v(-7.76, 18.73) * mm, "end": v(-7.77, 18.75) * mm});
            skLineSegment(sketch, "E373", {"start": v(-7.77, 18.75) * mm, "end": v(-7.78, 18.78) * mm});
            skLineSegment(sketch, "E374", {"start": v(-7.78, 18.78) * mm, "end": v(-7.8, 18.82) * mm});
            skLineSegment(sketch, "E375", {"start": v(-7.8, 18.82) * mm, "end": v(-7.83, 18.86) * mm});
            skLineSegment(sketch, "E376", {"start": v(-7.83, 18.86) * mm, "end": v(-7.86, 18.91) * mm});
            skLineSegment(sketch, "E377", {"start": v(-7.86, 18.91) * mm, "end": v(-7.9, 18.97) * mm});
            skLineSegment(sketch, "E378", {"start": v(-7.9, 18.97) * mm, "end": v(-7.94, 19.04) * mm});
            skLineSegment(sketch, "E379", {"start": v(-7.94, 19.04) * mm, "end": v(-7.99, 19.11) * mm});
            skLineSegment(sketch, "E380", {"start": v(-7.99, 19.11) * mm, "end": v(-8.05, 19.2) * mm});
            skLineSegment(sketch, "E381", {"start": v(-8.05, 19.2) * mm, "end": v(-8.11, 19.28) * mm});
            skLineSegment(sketch, "E382", {"start": v(-8.11, 19.28) * mm, "end": v(-8.18, 19.38) * mm});
            skLineSegment(sketch, "E383", {"start": v(-8.18, 19.38) * mm, "end": v(-8.26, 19.47) * mm});
            skLineSegment(sketch, "E384", {"start": v(-8.26, 19.47) * mm, "end": v(-8.35, 19.58) * mm});
            skLineSegment(sketch, "E385", {"start": v(-8.35, 19.58) * mm, "end": v(-8.45, 19.7) * mm});
            skLineSegment(sketch, "E386", {"start": v(-8.45, 19.7) * mm, "end": v(-8.56, 19.8) * mm});
            skLineSegment(sketch, "E387", {"start": v(-8.56, 19.8) * mm, "end": v(-8.68, 19.93) * mm});
            skLineSegment(sketch, "E388", {"start": v(-8.68, 19.93) * mm, "end": v(-8.8, 20.05) * mm});
            skLineSegment(sketch, "E389", {"start": v(-8.8, 20.05) * mm, "end": v(-8.94, 20.18) * mm});
            skLineSegment(sketch, "E390", {"start": v(-8.94, 20.18) * mm, "end": v(-9.08, 20.3) * mm});
            skLineSegment(sketch, "E391", {"start": v(-9.08, 20.3) * mm, "end": v(-9.24, 20.44) * mm});
            skLineSegment(sketch, "E392", {"start": v(-9.24, 20.44) * mm, "end": v(-9.4, 20.58) * mm});
            skLineSegment(sketch, "E393", {"start": v(-9.4, 20.58) * mm, "end": v(-9.58, 20.72) * mm});
            skLineSegment(sketch, "E394", {"start": v(-9.58, 20.72) * mm, "end": v(-9.76, 20.86) * mm});
            skLineSegment(sketch, "E395", {"start": v(-9.76, 20.86) * mm, "end": v(-9.96, 21) * mm});
            skLineSegment(sketch, "E396", {"start": v(-9.96, 21) * mm, "end": v(-10.17, 21.15) * mm});
            skLineSegment(sketch, "E397", {"start": v(-10.17, 21.15) * mm, "end": v(-10.4, 21.3) * mm});
            skLineSegment(sketch, "E398", {"start": v(-10.4, 21.3) * mm, "end": v(-10.62, 21.44) * mm});
            skLineSegment(sketch, "E399", {"start": v(-10.62, 21.44) * mm, "end": v(-10.86, 21.58) * mm});
            skLineSegment(sketch, "E400", {"start": v(-10.86, 21.58) * mm, "end": v(-11.12, 21.73) * mm});
            skLineSegment(sketch, "E401", {"start": v(-11.12, 21.73) * mm, "end": v(-11.38, 21.87) * mm});
            skLineSegment(sketch, "E402", {"start": v(-11.38, 21.87) * mm, "end": v(-11.66, 22.01) * mm});
            skLineSegment(sketch, "E403", {"start": v(-11.66, 22.01) * mm, "end": v(-11.95, 22.15) * mm});
            skLineSegment(sketch, "E404", {"start": v(-11.95, 22.15) * mm, "end": v(-12.25, 22.29) * mm});
            skLineSegment(sketch, "E405", {"start": v(-12.25, 22.29) * mm, "end": v(-12.5, 22.31) * mm});
            skLineSegment(sketch, "E406", {"start": v(-12.5, 22.31) * mm, "end": v(-13.21, 21.9) * mm});
            skLineSegment(sketch, "E407", {"start": v(-13.21, 21.9) * mm, "end": v(-13.31, 21.67) * mm});
            skLineSegment(sketch, "E408", {"start": v(-13.31, 21.67) * mm, "end": v(-13.34, 21.34) * mm});
            skLineSegment(sketch, "E409", {"start": v(-13.34, 21.34) * mm, "end": v(-13.36, 21.02) * mm});
            skLineSegment(sketch, "E410", {"start": v(-13.36, 21.02) * mm, "end": v(-13.38, 20.71) * mm});
            skLineSegment(sketch, "E411", {"start": v(-13.38, 20.71) * mm, "end": v(-13.38, 20.4) * mm});
            skLineSegment(sketch, "E412", {"start": v(-13.38, 20.4) * mm, "end": v(-13.38, 20.12) * mm});
            skLineSegment(sketch, "E413", {"start": v(-13.38, 20.12) * mm, "end": v(-13.38, 19.83) * mm});
            skLineSegment(sketch, "E414", {"start": v(-13.38, 19.83) * mm, "end": v(-13.37, 19.56) * mm});
            skLineSegment(sketch, "E415", {"start": v(-13.37, 19.56) * mm, "end": v(-13.35, 19.3) * mm});
            skLineSegment(sketch, "E416", {"start": v(-13.35, 19.3) * mm, "end": v(-13.33, 19.05) * mm});
            skLineSegment(sketch, "E417", {"start": v(-13.33, 19.05) * mm, "end": v(-13.3, 18.8) * mm});
            skLineSegment(sketch, "E418", {"start": v(-13.3, 18.8) * mm, "end": v(-13.27, 18.57) * mm});
            skLineSegment(sketch, "E419", {"start": v(-13.27, 18.57) * mm, "end": v(-13.24, 18.35) * mm});
            skLineSegment(sketch, "E420", {"start": v(-13.24, 18.35) * mm, "end": v(-13.2, 18.14) * mm});
            skLineSegment(sketch, "E421", {"start": v(-13.2, 18.14) * mm, "end": v(-13.16, 17.94) * mm});
            skLineSegment(sketch, "E422", {"start": v(-13.16, 17.94) * mm, "end": v(-13.12, 17.75) * mm});
            skLineSegment(sketch, "E423", {"start": v(-13.12, 17.75) * mm, "end": v(-13.07, 17.56) * mm});
            skLineSegment(sketch, "E424", {"start": v(-13.07, 17.56) * mm, "end": v(-13.03, 17.4) * mm});
            skLineSegment(sketch, "E425", {"start": v(-13.03, 17.4) * mm, "end": v(-12.98, 17.23) * mm});
            skLineSegment(sketch, "E426", {"start": v(-12.98, 17.23) * mm, "end": v(-12.93, 17.08) * mm});
            skLineSegment(sketch, "E427", {"start": v(-12.93, 17.08) * mm, "end": v(-12.89, 16.94) * mm});
            skLineSegment(sketch, "E428", {"start": v(-12.89, 16.94) * mm, "end": v(-12.84, 16.82) * mm});
            skLineSegment(sketch, "E429", {"start": v(-12.84, 16.82) * mm, "end": v(-12.8, 16.7) * mm});
            skLineSegment(sketch, "E430", {"start": v(-12.8, 16.7) * mm, "end": v(-12.75, 16.59) * mm});
            skLineSegment(sketch, "E431", {"start": v(-12.75, 16.59) * mm, "end": v(-12.7, 16.49) * mm});
            skLineSegment(sketch, "E432", {"start": v(-12.7, 16.49) * mm, "end": v(-12.66, 16.4) * mm});
            skLineSegment(sketch, "E433", {"start": v(-12.66, 16.4) * mm, "end": v(-12.62, 16.32) * mm});
            skLineSegment(sketch, "E434", {"start": v(-12.62, 16.32) * mm, "end": v(-12.58, 16.24) * mm});
            skLineSegment(sketch, "E435", {"start": v(-12.58, 16.24) * mm, "end": v(-12.55, 16.18) * mm});
            skLineSegment(sketch, "E436", {"start": v(-12.55, 16.18) * mm, "end": v(-12.52, 16.13) * mm});
            skLineSegment(sketch, "E437", {"start": v(-12.52, 16.13) * mm, "end": v(-12.5, 16.09) * mm});
            skLineSegment(sketch, "E438", {"start": v(-12.5, 16.09) * mm, "end": v(-12.47, 16.05) * mm});
            skLineSegment(sketch, "E439", {"start": v(-12.47, 16.05) * mm, "end": v(-12.45, 16.03) * mm});
            skLineSegment(sketch, "E440", {"start": v(-12.45, 16.03) * mm, "end": v(-12.44, 16) * mm});
            skLineSegment(sketch, "E441", {"start": v(-12.44, 16) * mm, "end": v(-12.43, 16) * mm});
            skLineSegment(sketch, "E442", {"start": v(-12.43, 16) * mm, "end": v(-11.95, 15.37) * mm});
            skLineSegment(sketch, "E443", {"start": v(-11.95, 15.37) * mm, "end": v(-13.77, 13.77) * mm});
            skLineSegment(sketch, "E444", {"start": v(-13.77, 13.77) * mm, "end": v(-14.33, 14.33) * mm});
            skLineSegment(sketch, "E445", {"start": v(-14.33, 14.33) * mm, "end": v(-14.34, 14.34) * mm});
            skLineSegment(sketch, "E446", {"start": v(-14.34, 14.34) * mm, "end": v(-14.35, 14.35) * mm});
            skLineSegment(sketch, "E447", {"start": v(-14.35, 14.35) * mm, "end": v(-14.38, 14.37) * mm});
            skLineSegment(sketch, "E448", {"start": v(-14.38, 14.37) * mm, "end": v(-14.4, 14.4) * mm});
            skLineSegment(sketch, "E449", {"start": v(-14.4, 14.4) * mm, "end": v(-14.45, 14.43) * mm});
            skLineSegment(sketch, "E450", {"start": v(-14.45, 14.43) * mm, "end": v(-14.5, 14.47) * mm});
            skLineSegment(sketch, "E451", {"start": v(-14.5, 14.47) * mm, "end": v(-14.55, 14.5) * mm});
            skLineSegment(sketch, "E452", {"start": v(-14.55, 14.5) * mm, "end": v(-14.62, 14.55) * mm});
            skLineSegment(sketch, "E453", {"start": v(-14.62, 14.55) * mm, "end": v(-14.7, 14.6) * mm});
            skLineSegment(sketch, "E454", {"start": v(-14.7, 14.6) * mm, "end": v(-14.78, 14.65) * mm});
            skLineSegment(sketch, "E455", {"start": v(-14.78, 14.65) * mm, "end": v(-14.87, 14.71) * mm});
            skLineSegment(sketch, "E456", {"start": v(-14.87, 14.71) * mm, "end": v(-14.98, 14.77) * mm});
            skLineSegment(sketch, "E457", {"start": v(-14.98, 14.77) * mm, "end": v(-15.09, 14.83) * mm});
            skLineSegment(sketch, "E458", {"start": v(-15.09, 14.83) * mm, "end": v(-15.21, 14.9) * mm});
            skLineSegment(sketch, "E459", {"start": v(-15.21, 14.9) * mm, "end": v(-15.34, 14.96) * mm});
            skLineSegment(sketch, "E460", {"start": v(-15.34, 14.96) * mm, "end": v(-15.49, 15.02) * mm});
            skLineSegment(sketch, "E461", {"start": v(-15.49, 15.02) * mm, "end": v(-15.64, 15.09) * mm});
            skLineSegment(sketch, "E462", {"start": v(-15.64, 15.09) * mm, "end": v(-15.8, 15.15) * mm});
            skLineSegment(sketch, "E463", {"start": v(-15.8, 15.15) * mm, "end": v(-15.98, 15.22) * mm});
            skLineSegment(sketch, "E464", {"start": v(-15.98, 15.22) * mm, "end": v(-16.16, 15.29) * mm});
            skLineSegment(sketch, "E465", {"start": v(-16.16, 15.29) * mm, "end": v(-16.36, 15.35) * mm});
            skLineSegment(sketch, "E466", {"start": v(-16.36, 15.35) * mm, "end": v(-16.56, 15.42) * mm});
            skLineSegment(sketch, "E467", {"start": v(-16.56, 15.42) * mm, "end": v(-16.78, 15.48) * mm});
            skLineSegment(sketch, "E468", {"start": v(-16.78, 15.48) * mm, "end": v(-17, 15.54) * mm});
            skLineSegment(sketch, "E469", {"start": v(-17, 15.54) * mm, "end": v(-17.24, 15.6) * mm});
            skLineSegment(sketch, "E470", {"start": v(-17.24, 15.6) * mm, "end": v(-17.49, 15.65) * mm});
            skLineSegment(sketch, "E471", {"start": v(-17.49, 15.65) * mm, "end": v(-17.75, 15.7) * mm});
            skLineSegment(sketch, "E472", {"start": v(-17.75, 15.7) * mm, "end": v(-18.02, 15.74) * mm});
            skLineSegment(sketch, "E473", {"start": v(-18.02, 15.74) * mm, "end": v(-18.3, 15.78) * mm});
            skLineSegment(sketch, "E474", {"start": v(-18.3, 15.78) * mm, "end": v(-18.59, 15.82) * mm});
            skLineSegment(sketch, "E475", {"start": v(-18.59, 15.82) * mm, "end": v(-18.89, 15.85) * mm});
            skLineSegment(sketch, "E476", {"start": v(-18.89, 15.85) * mm, "end": v(-19.2, 15.87) * mm});
            skLineSegment(sketch, "E477", {"start": v(-19.2, 15.87) * mm, "end": v(-19.52, 15.9) * mm});
            skLineSegment(sketch, "E478", {"start": v(-19.52, 15.9) * mm, "end": v(-19.85, 15.9) * mm});
            skLineSegment(sketch, "E479", {"start": v(-19.85, 15.9) * mm, "end": v(-20.09, 15.83) * mm});
            skLineSegment(sketch, "E480", {"start": v(-20.09, 15.83) * mm, "end": v(-20.59, 15.18) * mm});
            skLineSegment(sketch, "E481", {"start": v(-20.59, 15.18) * mm, "end": v(-20.6, 14.93) * mm});
            skLineSegment(sketch, "E482", {"start": v(-20.6, 14.93) * mm, "end": v(-20.5, 14.61) * mm});
            skLineSegment(sketch, "E483", {"start": v(-20.5, 14.61) * mm, "end": v(-20.4, 14.3) * mm});
            skLineSegment(sketch, "E484", {"start": v(-20.4, 14.3) * mm, "end": v(-20.28, 14.02) * mm});
            skLineSegment(sketch, "E485", {"start": v(-20.28, 14.02) * mm, "end": v(-20.18, 13.73) * mm});
            skLineSegment(sketch, "E486", {"start": v(-20.18, 13.73) * mm, "end": v(-20.06, 13.46) * mm});
            skLineSegment(sketch, "E487", {"start": v(-20.06, 13.46) * mm, "end": v(-19.95, 13.2) * mm});
            skLineSegment(sketch, "E488", {"start": v(-19.95, 13.2) * mm, "end": v(-19.83, 12.96) * mm});
            skLineSegment(sketch, "E489", {"start": v(-19.83, 12.96) * mm, "end": v(-19.72, 12.72) * mm});
            skLineSegment(sketch, "E490", {"start": v(-19.72, 12.72) * mm, "end": v(-19.6, 12.5) * mm});
            skLineSegment(sketch, "E491", {"start": v(-19.6, 12.5) * mm, "end": v(-19.48, 12.28) * mm});
            skLineSegment(sketch, "E492", {"start": v(-19.48, 12.28) * mm, "end": v(-19.37, 12.08) * mm});
            skLineSegment(sketch, "E493", {"start": v(-19.37, 12.08) * mm, "end": v(-19.25, 11.89) * mm});
            skLineSegment(sketch, "E494", {"start": v(-19.25, 11.89) * mm, "end": v(-19.14, 11.7) * mm});
            skLineSegment(sketch, "E495", {"start": v(-19.14, 11.7) * mm, "end": v(-19.02, 11.54) * mm});
            skLineSegment(sketch, "E496", {"start": v(-19.02, 11.54) * mm, "end": v(-18.9, 11.38) * mm});
            skLineSegment(sketch, "E497", {"start": v(-18.9, 11.38) * mm, "end": v(-18.8, 11.23) * mm});
            skLineSegment(sketch, "E498", {"start": v(-18.8, 11.23) * mm, "end": v(-18.7, 11.09) * mm});
            skLineSegment(sketch, "E499", {"start": v(-18.7, 11.09) * mm, "end": v(-18.59, 10.96) * mm});
            skLineSegment(sketch, "E500", {"start": v(-18.59, 10.96) * mm, "end": v(-18.49, 10.83) * mm});
            skLineSegment(sketch, "E501", {"start": v(-18.49, 10.83) * mm, "end": v(-18.39, 10.72) * mm});
            skLineSegment(sketch, "E502", {"start": v(-18.39, 10.72) * mm, "end": v(-18.3, 10.62) * mm});
            skLineSegment(sketch, "E503", {"start": v(-18.3, 10.62) * mm, "end": v(-18.2, 10.53) * mm});
            skLineSegment(sketch, "E504", {"start": v(-18.2, 10.53) * mm, "end": v(-18.12, 10.45) * mm});
            skLineSegment(sketch, "E505", {"start": v(-18.12, 10.45) * mm, "end": v(-18.04, 10.37) * mm});
            skLineSegment(sketch, "E506", {"start": v(-18.04, 10.37) * mm, "end": v(-17.97, 10.3) * mm});
            skLineSegment(sketch, "E507", {"start": v(-17.97, 10.3) * mm, "end": v(-17.9, 10.24) * mm});
            skLineSegment(sketch, "E508", {"start": v(-17.9, 10.24) * mm, "end": v(-17.84, 10.2) * mm});
            skLineSegment(sketch, "E509", {"start": v(-17.84, 10.2) * mm, "end": v(-17.79, 10.15) * mm});
            skLineSegment(sketch, "E510", {"start": v(-17.79, 10.15) * mm, "end": v(-17.74, 10.11) * mm});
            skLineSegment(sketch, "E511", {"start": v(-17.74, 10.11) * mm, "end": v(-17.7, 10.08) * mm});
            skLineSegment(sketch, "E512", {"start": v(-17.7, 10.08) * mm, "end": v(-17.67, 10.06) * mm});
            skLineSegment(sketch, "E513", {"start": v(-17.67, 10.06) * mm, "end": v(-17.64, 10.04) * mm});
            skLineSegment(sketch, "E514", {"start": v(-17.64, 10.04) * mm, "end": v(-17.62, 10.03) * mm});
            skLineSegment(sketch, "E515", {"start": v(-17.62, 10.03) * mm, "end": v(-17.6, 10.02) * mm});
            skLineSegment(sketch, "E516", {"start": v(-17.6, 10.02) * mm, "end": v(-16.92, 9.63) * mm});
            skLineSegment(sketch, "E517", {"start": v(-16.92, 9.63) * mm, "end": v(-17.99, 7.45) * mm});
            skLineSegment(sketch, "E518", {"start": v(-17.99, 7.45) * mm, "end": v(-18.72, 7.75) * mm});
            skLineSegment(sketch, "E519", {"start": v(-18.72, 7.75) * mm, "end": v(-18.73, 7.76) * mm});
            skLineSegment(sketch, "E520", {"start": v(-18.73, 7.76) * mm, "end": v(-18.75, 7.77) * mm});
            skLineSegment(sketch, "E521", {"start": v(-18.75, 7.77) * mm, "end": v(-18.78, 7.78) * mm});
            skLineSegment(sketch, "E522", {"start": v(-18.78, 7.78) * mm, "end": v(-18.82, 7.79) * mm});
            skLineSegment(sketch, "E523", {"start": v(-18.82, 7.79) * mm, "end": v(-18.87, 7.8) * mm});
            skLineSegment(sketch, "E524", {"start": v(-18.87, 7.8) * mm, "end": v(-18.93, 7.82) * mm});
            skLineSegment(sketch, "E525", {"start": v(-18.93, 7.82) * mm, "end": v(-19, 7.83) * mm});
            skLineSegment(sketch, "E526", {"start": v(-19, 7.83) * mm, "end": v(-19.08, 7.85) * mm});
            skLineSegment(sketch, "E527", {"start": v(-19.08, 7.85) * mm, "end": v(-19.16, 7.87) * mm});
            skLineSegment(sketch, "E528", {"start": v(-19.16, 7.87) * mm, "end": v(-19.26, 7.88) * mm});
            skLineSegment(sketch, "E529", {"start": v(-19.26, 7.88) * mm, "end": v(-19.37, 7.9) * mm});
            skLineSegment(sketch, "E530", {"start": v(-19.37, 7.9) * mm, "end": v(-19.49, 7.91) * mm});
            skLineSegment(sketch, "E531", {"start": v(-19.49, 7.91) * mm, "end": v(-19.61, 7.93) * mm});
            skLineSegment(sketch, "E532", {"start": v(-19.61, 7.93) * mm, "end": v(-19.75, 7.94) * mm});
            skLineSegment(sketch, "E533", {"start": v(-19.75, 7.94) * mm, "end": v(-19.9, 7.95) * mm});
            skLineSegment(sketch, "E534", {"start": v(-19.9, 7.95) * mm, "end": v(-20.06, 7.95) * mm});
            skLineSegment(sketch, "E535", {"start": v(-20.06, 7.95) * mm, "end": v(-20.22, 7.96) * mm});
            skLineSegment(sketch, "E536", {"start": v(-20.22, 7.96) * mm, "end": v(-20.4, 7.95) * mm});
            skLineSegment(sketch, "E537", {"start": v(-20.4, 7.95) * mm, "end": v(-20.59, 7.95) * mm});
            skLineSegment(sketch, "E538", {"start": v(-20.59, 7.95) * mm, "end": v(-20.78, 7.94) * mm});
            skLineSegment(sketch, "E539", {"start": v(-20.78, 7.94) * mm, "end": v(-20.99, 7.92) * mm});
            skLineSegment(sketch, "E540", {"start": v(-20.99, 7.92) * mm, "end": v(-21.2, 7.9) * mm});
            skLineSegment(sketch, "E541", {"start": v(-21.2, 7.9) * mm, "end": v(-21.42, 7.88) * mm});
            skLineSegment(sketch, "E542", {"start": v(-21.42, 7.88) * mm, "end": v(-21.66, 7.85) * mm});
            skLineSegment(sketch, "E543", {"start": v(-21.66, 7.85) * mm, "end": v(-21.9, 7.8) * mm});
            skLineSegment(sketch, "E544", {"start": v(-21.9, 7.8) * mm, "end": v(-22.15, 7.76) * mm});
            skLineSegment(sketch, "E545", {"start": v(-22.15, 7.76) * mm, "end": v(-22.4, 7.7) * mm});
            skLineSegment(sketch, "E546", {"start": v(-22.4, 7.7) * mm, "end": v(-22.67, 7.65) * mm});
            skLineSegment(sketch, "E547", {"start": v(-22.67, 7.65) * mm, "end": v(-22.94, 7.58) * mm});
            skLineSegment(sketch, "E548", {"start": v(-22.94, 7.58) * mm, "end": v(-23.22, 7.5) * mm});
            skLineSegment(sketch, "E549", {"start": v(-23.22, 7.5) * mm, "end": v(-23.51, 7.41) * mm});
            skLineSegment(sketch, "E550", {"start": v(-23.51, 7.41) * mm, "end": v(-23.81, 7.32) * mm});
            skLineSegment(sketch, "E551", {"start": v(-23.81, 7.32) * mm, "end": v(-24.11, 7.21) * mm});
            skLineSegment(sketch, "E552", {"start": v(-24.11, 7.21) * mm, "end": v(-24.42, 7.1) * mm});
            skLineSegment(sketch, "E553", {"start": v(-24.42, 7.1) * mm, "end": v(-24.62, 6.94) * mm});
            skLineSegment(sketch, "E554", {"start": v(-24.62, 6.94) * mm, "end": v(-24.83, 6.15) * mm});
            skLineSegment(sketch, "E555", {"start": v(-24.83, 6.15) * mm, "end": v(-24.74, 5.91) * mm});
            skLineSegment(sketch, "E556", {"start": v(-24.74, 5.91) * mm, "end": v(-24.53, 5.66) * mm});
            skLineSegment(sketch, "E557", {"start": v(-24.53, 5.66) * mm, "end": v(-24.31, 5.42) * mm});
            skLineSegment(sketch, "E558", {"start": v(-24.31, 5.42) * mm, "end": v(-24.1, 5.19) * mm});
            skLineSegment(sketch, "E559", {"start": v(-24.1, 5.19) * mm, "end": v(-23.9, 4.97) * mm});
            skLineSegment(sketch, "E560", {"start": v(-23.9, 4.97) * mm, "end": v(-23.69, 4.76) * mm});
            skLineSegment(sketch, "E561", {"start": v(-23.69, 4.76) * mm, "end": v(-23.48, 4.57) * mm});
            skLineSegment(sketch, "E562", {"start": v(-23.48, 4.57) * mm, "end": v(-23.28, 4.38) * mm});
            skLineSegment(sketch, "E563", {"start": v(-23.28, 4.38) * mm, "end": v(-23.09, 4.2) * mm});
            skLineSegment(sketch, "E564", {"start": v(-23.09, 4.2) * mm, "end": v(-22.9, 4.04) * mm});
            skLineSegment(sketch, "E565", {"start": v(-22.9, 4.04) * mm, "end": v(-22.7, 3.9) * mm});
            skLineSegment(sketch, "E566", {"start": v(-22.7, 3.9) * mm, "end": v(-22.52, 3.75) * mm});
            skLineSegment(sketch, "E567", {"start": v(-22.52, 3.75) * mm, "end": v(-22.33, 3.62) * mm});
            skLineSegment(sketch, "E568", {"start": v(-22.33, 3.62) * mm, "end": v(-22.16, 3.5) * mm});
            skLineSegment(sketch, "E569", {"start": v(-22.16, 3.5) * mm, "end": v(-21.99, 3.38) * mm});
            skLineSegment(sketch, "E570", {"start": v(-21.99, 3.38) * mm, "end": v(-21.82, 3.27) * mm});
            skLineSegment(sketch, "E571", {"start": v(-21.82, 3.27) * mm, "end": v(-21.66, 3.18) * mm});
            skLineSegment(sketch, "E572", {"start": v(-21.66, 3.18) * mm, "end": v(-21.51, 3.09) * mm});
            skLineSegment(sketch, "E573", {"start": v(-21.51, 3.09) * mm, "end": v(-21.36, 3) * mm});
            skLineSegment(sketch, "E574", {"start": v(-21.36, 3) * mm, "end": v(-21.23, 2.94) * mm});
            skLineSegment(sketch, "E575", {"start": v(-21.23, 2.94) * mm, "end": v(-21.1, 2.87) * mm});
            skLineSegment(sketch, "E576", {"start": v(-21.1, 2.87) * mm, "end": v(-20.97, 2.81) * mm});
            skLineSegment(sketch, "E577", {"start": v(-20.97, 2.81) * mm, "end": v(-20.85, 2.76) * mm});
            skLineSegment(sketch, "E578", {"start": v(-20.85, 2.76) * mm, "end": v(-20.74, 2.71) * mm});
            skLineSegment(sketch, "E579", {"start": v(-20.74, 2.71) * mm, "end": v(-20.64, 2.67) * mm});
            skLineSegment(sketch, "E580", {"start": v(-20.64, 2.67) * mm, "end": v(-20.55, 2.64) * mm});
            skLineSegment(sketch, "E581", {"start": v(-20.55, 2.64) * mm, "end": v(-20.46, 2.61) * mm});
            skLineSegment(sketch, "E582", {"start": v(-20.46, 2.61) * mm, "end": v(-20.39, 2.59) * mm});
            skLineSegment(sketch, "E583", {"start": v(-20.39, 2.59) * mm, "end": v(-20.32, 2.57) * mm});
            skLineSegment(sketch, "E584", {"start": v(-20.32, 2.57) * mm, "end": v(-20.26, 2.55) * mm});
            skLineSegment(sketch, "E585", {"start": v(-20.26, 2.55) * mm, "end": v(-20.2, 2.54) * mm});
            skLineSegment(sketch, "E586", {"start": v(-20.2, 2.54) * mm, "end": v(-20.17, 2.53) * mm});
            skLineSegment(sketch, "E587", {"start": v(-20.17, 2.53) * mm, "end": v(-20.14, 2.53) * mm});
            skLineSegment(sketch, "E588", {"start": v(-20.14, 2.53) * mm, "end": v(-20.12, 2.52) * mm});
            skLineSegment(sketch, "E589", {"start": v(-20.12, 2.52) * mm, "end": v(-20.1, 2.52) * mm});
            skLineSegment(sketch, "E590", {"start": v(-20.1, 2.52) * mm, "end": v(-19.32, 2.42) * mm});
            skLineSegment(sketch, "E591", {"start": v(-19.32, 2.42) * mm, "end": v(-19.47, 0) * mm});
            skLineSegment(sketch, "E592", {"start": v(-19.47, 0) * mm, "end": v(-20.26, 0) * mm});
            skLineSegment(sketch, "E593", {"start": v(-20.26, 0) * mm, "end": v(-20.27, 0) * mm});
            skLineSegment(sketch, "E594", {"start": v(-20.27, 0) * mm, "end": v(-20.3, 0) * mm});
            skLineSegment(sketch, "E595", {"start": v(-20.3, 0) * mm, "end": v(-20.33, 0) * mm});
            skLineSegment(sketch, "E596", {"start": v(-20.33, 0) * mm, "end": v(-20.37, 0) * mm});
            skLineSegment(sketch, "E597", {"start": v(-20.37, 0) * mm, "end": v(-20.42, -0.01) * mm});
            skLineSegment(sketch, "E598", {"start": v(-20.42, -0.01) * mm, "end": v(-20.48, -0.02) * mm});
            skLineSegment(sketch, "E599", {"start": v(-20.48, -0.02) * mm, "end": v(-20.55, -0.03) * mm});
            skLineSegment(sketch, "E600", {"start": v(-20.55, -0.03) * mm, "end": v(-20.63, -0.05) * mm});
            skLineSegment(sketch, "E601", {"start": v(-20.63, -0.05) * mm, "end": v(-20.72, -0.07) * mm});
            skLineSegment(sketch, "E602", {"start": v(-20.72, -0.07) * mm, "end": v(-20.81, -0.09) * mm});
            skLineSegment(sketch, "E603", {"start": v(-20.81, -0.09) * mm, "end": v(-20.92, -0.11) * mm});
            skLineSegment(sketch, "E604", {"start": v(-20.92, -0.11) * mm, "end": v(-21.03, -0.15) * mm});
            skLineSegment(sketch, "E605", {"start": v(-21.03, -0.15) * mm, "end": v(-21.15, -0.18) * mm});
            skLineSegment(sketch, "E606", {"start": v(-21.15, -0.18) * mm, "end": v(-21.29, -0.22) * mm});
            skLineSegment(sketch, "E607", {"start": v(-21.29, -0.22) * mm, "end": v(-21.43, -0.27) * mm});
            skLineSegment(sketch, "E608", {"start": v(-21.43, -0.27) * mm, "end": v(-21.57, -0.33) * mm});
            skLineSegment(sketch, "E609", {"start": v(-21.57, -0.33) * mm, "end": v(-21.73, -0.39) * mm});
            skLineSegment(sketch, "E610", {"start": v(-21.73, -0.39) * mm, "end": v(-21.9, -0.46) * mm});
            skLineSegment(sketch, "E611", {"start": v(-21.9, -0.46) * mm, "end": v(-22.06, -0.53) * mm});
            skLineSegment(sketch, "E612", {"start": v(-22.06, -0.53) * mm, "end": v(-22.24, -0.62) * mm});
            skLineSegment(sketch, "E613", {"start": v(-22.24, -0.62) * mm, "end": v(-22.42, -0.7) * mm});
            skLineSegment(sketch, "E614", {"start": v(-22.42, -0.7) * mm, "end": v(-22.61, -0.81) * mm});
            skLineSegment(sketch, "E615", {"start": v(-22.61, -0.81) * mm, "end": v(-22.8, -0.92) * mm});
            skLineSegment(sketch, "E616", {"start": v(-22.8, -0.92) * mm, "end": v(-23, -1.04) * mm});
            skLineSegment(sketch, "E617", {"start": v(-23, -1.04) * mm, "end": v(-23.22, -1.17) * mm});
            skLineSegment(sketch, "E618", {"start": v(-23.22, -1.17) * mm, "end": v(-23.43, -1.3) * mm});
            skLineSegment(sketch, "E619", {"start": v(-23.43, -1.3) * mm, "end": v(-23.65, -1.45) * mm});
            skLineSegment(sketch, "E620", {"start": v(-23.65, -1.45) * mm, "end": v(-23.87, -1.6) * mm});
            skLineSegment(sketch, "E621", {"start": v(-23.87, -1.6) * mm, "end": v(-24.1, -1.78) * mm});
            skLineSegment(sketch, "E622", {"start": v(-24.1, -1.78) * mm, "end": v(-24.33, -1.96) * mm});
            skLineSegment(sketch, "E623", {"start": v(-24.33, -1.96) * mm, "end": v(-24.56, -2.15) * mm});
            skLineSegment(sketch, "E624", {"start": v(-24.56, -2.15) * mm, "end": v(-24.8, -2.35) * mm});
            skLineSegment(sketch, "E625", {"start": v(-24.8, -2.35) * mm, "end": v(-25.04, -2.56) * mm});
            skLineSegment(sketch, "E626", {"start": v(-25.04, -2.56) * mm, "end": v(-25.28, -2.79) * mm});
            skLineSegment(sketch, "E627", {"start": v(-25.28, -2.79) * mm, "end": v(-25.4, -3.01) * mm});
            skLineSegment(sketch, "E628", {"start": v(-25.4, -3.01) * mm, "end": v(-25.3, -3.82) * mm});
            skLineSegment(sketch, "E629", {"start": v(-25.3, -3.82) * mm, "end": v(-25.12, -4) * mm});
            skLineSegment(sketch, "E630", {"start": v(-25.12, -4) * mm, "end": v(-24.82, -4.16) * mm});
            skLineSegment(sketch, "E631", {"start": v(-24.82, -4.16) * mm, "end": v(-24.54, -4.3) * mm});
            skLineSegment(sketch, "E632", {"start": v(-24.54, -4.3) * mm, "end": v(-24.25, -4.43) * mm});
            skLineSegment(sketch, "E633", {"start": v(-24.25, -4.43) * mm, "end": v(-23.98, -4.55) * mm});
            skLineSegment(sketch, "E634", {"start": v(-23.98, -4.55) * mm, "end": v(-23.7, -4.67) * mm});
            skLineSegment(sketch, "E635", {"start": v(-23.7, -4.67) * mm, "end": v(-23.44, -4.77) * mm});
            skLineSegment(sketch, "E636", {"start": v(-23.44, -4.77) * mm, "end": v(-23.19, -4.86) * mm});
            skLineSegment(sketch, "E637", {"start": v(-23.19, -4.86) * mm, "end": v(-22.94, -4.95) * mm});
            skLineSegment(sketch, "E638", {"start": v(-22.94, -4.95) * mm, "end": v(-22.7, -5.02) * mm});
            skLineSegment(sketch, "E639", {"start": v(-22.7, -5.02) * mm, "end": v(-22.46, -5.1) * mm});
            skLineSegment(sketch, "E640", {"start": v(-22.46, -5.1) * mm, "end": v(-22.24, -5.15) * mm});
            skLineSegment(sketch, "E641", {"start": v(-22.24, -5.15) * mm, "end": v(-22.02, -5.2) * mm});
            skLineSegment(sketch, "E642", {"start": v(-22.02, -5.2) * mm, "end": v(-21.8, -5.25) * mm});
            skLineSegment(sketch, "E643", {"start": v(-21.8, -5.25) * mm, "end": v(-21.6, -5.3) * mm});
            skLineSegment(sketch, "E644", {"start": v(-21.6, -5.3) * mm, "end": v(-21.41, -5.33) * mm});
            skLineSegment(sketch, "E645", {"start": v(-21.41, -5.33) * mm, "end": v(-21.23, -5.36) * mm});
            skLineSegment(sketch, "E646", {"start": v(-21.23, -5.36) * mm, "end": v(-21.06, -5.38) * mm});
            skLineSegment(sketch, "E647", {"start": v(-21.06, -5.38) * mm, "end": v(-20.89, -5.4) * mm});
            skLineSegment(sketch, "E648", {"start": v(-20.89, -5.4) * mm, "end": v(-20.73, -5.41) * mm});
            skLineSegment(sketch, "E649", {"start": v(-20.73, -5.41) * mm, "end": v(-20.59, -5.42) * mm});
            skLineSegment(sketch, "E650", {"start": v(-20.59, -5.42) * mm, "end": v(-20.45, -5.43) * mm});
            skLineSegment(sketch, "E651", {"start": v(-20.45, -5.43) * mm, "end": v(-20.32, -5.43) * mm});
            skLineSegment(sketch, "E652", {"start": v(-20.32, -5.43) * mm, "end": v(-20.2, -5.43) * mm});
            skLineSegment(sketch, "E653", {"start": v(-20.2, -5.43) * mm, "end": v(-20.1, -5.43) * mm});
            skLineSegment(sketch, "E654", {"start": v(-20.1, -5.43) * mm, "end": v(-20, -5.42) * mm});
            skLineSegment(sketch, "E655", {"start": v(-20, -5.42) * mm, "end": v(-19.9, -5.42) * mm});
            skLineSegment(sketch, "E656", {"start": v(-19.9, -5.42) * mm, "end": v(-19.82, -5.4) * mm});
            skLineSegment(sketch, "E657", {"start": v(-19.82, -5.4) * mm, "end": v(-19.75, -5.4) * mm});
            skLineSegment(sketch, "E658", {"start": v(-19.75, -5.4) * mm, "end": v(-19.7, -5.4) * mm});
            skLineSegment(sketch, "E659", {"start": v(-19.7, -5.4) * mm, "end": v(-19.64, -5.39) * mm});
            skLineSegment(sketch, "E660", {"start": v(-19.64, -5.39) * mm, "end": v(-19.6, -5.38) * mm});
            skLineSegment(sketch, "E661", {"start": v(-19.6, -5.38) * mm, "end": v(-19.57, -5.37) * mm});
            skLineSegment(sketch, "E662", {"start": v(-19.57, -5.37) * mm, "end": v(-19.55, -5.37) * mm});
            skLineSegment(sketch, "E663", {"start": v(-19.55, -5.37) * mm, "end": v(-19.54, -5.37) * mm});
            skLineSegment(sketch, "E664", {"start": v(-19.54, -5.37) * mm, "end": v(-18.77, -5.16) * mm});
            skLineSegment(sketch, "E665", {"start": v(-18.77, -5.16) * mm, "end": v(-17.99, -7.45) * mm});
            skLineSegment(sketch, "E666", {"start": v(-17.99, -7.45) * mm, "end": v(-18.72, -7.75) * mm});
            skLineSegment(sketch, "E667", {"start": v(-18.72, -7.75) * mm, "end": v(-18.73, -7.76) * mm});
            skLineSegment(sketch, "E668", {"start": v(-18.73, -7.76) * mm, "end": v(-18.75, -7.77) * mm});
            skLineSegment(sketch, "E669", {"start": v(-18.75, -7.77) * mm, "end": v(-18.78, -7.78) * mm});
            skLineSegment(sketch, "E670", {"start": v(-18.78, -7.78) * mm, "end": v(-18.81, -7.8) * mm});
            skLineSegment(sketch, "E671", {"start": v(-18.81, -7.8) * mm, "end": v(-18.86, -7.83) * mm});
            skLineSegment(sketch, "E672", {"start": v(-18.86, -7.83) * mm, "end": v(-18.91, -7.86) * mm});
            skLineSegment(sketch, "E673", {"start": v(-18.91, -7.86) * mm, "end": v(-18.97, -7.9) * mm});
            skLineSegment(sketch, "E674", {"start": v(-18.97, -7.9) * mm, "end": v(-19.04, -7.94) * mm});
            skLineSegment(sketch, "E675", {"start": v(-19.04, -7.94) * mm, "end": v(-19.11, -7.99) * mm});
            skLineSegment(sketch, "E676", {"start": v(-19.11, -7.99) * mm, "end": v(-19.2, -8.05) * mm});
            skLineSegment(sketch, "E677", {"start": v(-19.2, -8.05) * mm, "end": v(-19.28, -8.11) * mm});
            skLineSegment(sketch, "E678", {"start": v(-19.28, -8.11) * mm, "end": v(-19.38, -8.18) * mm});
            skLineSegment(sketch, "E679", {"start": v(-19.38, -8.18) * mm, "end": v(-19.47, -8.26) * mm});
            skLineSegment(sketch, "E680", {"start": v(-19.47, -8.26) * mm, "end": v(-19.58, -8.35) * mm});
            skLineSegment(sketch, "E681", {"start": v(-19.58, -8.35) * mm, "end": v(-19.7, -8.45) * mm});
            skLineSegment(sketch, "E682", {"start": v(-19.7, -8.45) * mm, "end": v(-19.8, -8.56) * mm});
            skLineSegment(sketch, "E683", {"start": v(-19.8, -8.56) * mm, "end": v(-19.93, -8.68) * mm});
            skLineSegment(sketch, "E684", {"start": v(-19.93, -8.68) * mm, "end": v(-20.05, -8.8) * mm});
            skLineSegment(sketch, "E685", {"start": v(-20.05, -8.8) * mm, "end": v(-20.18, -8.94) * mm});
            skLineSegment(sketch, "E686", {"start": v(-20.18, -8.94) * mm, "end": v(-20.3, -9.08) * mm});
            skLineSegment(sketch, "E687", {"start": v(-20.3, -9.08) * mm, "end": v(-20.44, -9.24) * mm});
            skLineSegment(sketch, "E688", {"start": v(-20.44, -9.24) * mm, "end": v(-20.58, -9.4) * mm});
            skLineSegment(sketch, "E689", {"start": v(-20.58, -9.4) * mm, "end": v(-20.72, -9.58) * mm});
            skLineSegment(sketch, "E690", {"start": v(-20.72, -9.58) * mm, "end": v(-20.86, -9.76) * mm});
            skLineSegment(sketch, "E691", {"start": v(-20.86, -9.76) * mm, "end": v(-21, -9.96) * mm});
            skLineSegment(sketch, "E692", {"start": v(-21, -9.96) * mm, "end": v(-21.15, -10.17) * mm});
            skLineSegment(sketch, "E693", {"start": v(-21.15, -10.17) * mm, "end": v(-21.3, -10.4) * mm});
            skLineSegment(sketch, "E694", {"start": v(-21.3, -10.4) * mm, "end": v(-21.44, -10.62) * mm});
            skLineSegment(sketch, "E695", {"start": v(-21.44, -10.62) * mm, "end": v(-21.58, -10.86) * mm});
            skLineSegment(sketch, "E696", {"start": v(-21.58, -10.86) * mm, "end": v(-21.73, -11.12) * mm});
            skLineSegment(sketch, "E697", {"start": v(-21.73, -11.12) * mm, "end": v(-21.87, -11.38) * mm});
            skLineSegment(sketch, "E698", {"start": v(-21.87, -11.38) * mm, "end": v(-22.01, -11.66) * mm});
            skLineSegment(sketch, "E699", {"start": v(-22.01, -11.66) * mm, "end": v(-22.15, -11.95) * mm});
            skLineSegment(sketch, "E700", {"start": v(-22.15, -11.95) * mm, "end": v(-22.29, -12.25) * mm});
            skLineSegment(sketch, "E701", {"start": v(-22.29, -12.25) * mm, "end": v(-22.31, -12.5) * mm});
            skLineSegment(sketch, "E702", {"start": v(-22.31, -12.5) * mm, "end": v(-21.9, -13.21) * mm});
            skLineSegment(sketch, "E703", {"start": v(-21.9, -13.21) * mm, "end": v(-21.67, -13.31) * mm});
            skLineSegment(sketch, "E704", {"start": v(-21.67, -13.31) * mm, "end": v(-21.34, -13.34) * mm});
            skLineSegment(sketch, "E705", {"start": v(-21.34, -13.34) * mm, "end": v(-21.02, -13.36) * mm});
            skLineSegment(sketch, "E706", {"start": v(-21.02, -13.36) * mm, "end": v(-20.71, -13.38) * mm});
            skLineSegment(sketch, "E707", {"start": v(-20.71, -13.38) * mm, "end": v(-20.4, -13.38) * mm});
            skLineSegment(sketch, "E708", {"start": v(-20.4, -13.38) * mm, "end": v(-20.12, -13.38) * mm});
            skLineSegment(sketch, "E709", {"start": v(-20.12, -13.38) * mm, "end": v(-19.83, -13.38) * mm});
            skLineSegment(sketch, "E710", {"start": v(-19.83, -13.38) * mm, "end": v(-19.56, -13.37) * mm});
            skLineSegment(sketch, "E711", {"start": v(-19.56, -13.37) * mm, "end": v(-19.3, -13.35) * mm});
            skLineSegment(sketch, "E712", {"start": v(-19.3, -13.35) * mm, "end": v(-19.05, -13.33) * mm});
            skLineSegment(sketch, "E713", {"start": v(-19.05, -13.33) * mm, "end": v(-18.8, -13.3) * mm});
            skLineSegment(sketch, "E714", {"start": v(-18.8, -13.3) * mm, "end": v(-18.57, -13.27) * mm});
            skLineSegment(sketch, "E715", {"start": v(-18.57, -13.27) * mm, "end": v(-18.35, -13.24) * mm});
            skLineSegment(sketch, "E716", {"start": v(-18.35, -13.24) * mm, "end": v(-18.14, -13.2) * mm});
            skLineSegment(sketch, "E717", {"start": v(-18.14, -13.2) * mm, "end": v(-17.94, -13.16) * mm});
            skLineSegment(sketch, "E718", {"start": v(-17.94, -13.16) * mm, "end": v(-17.75, -13.12) * mm});
            skLineSegment(sketch, "E719", {"start": v(-17.75, -13.12) * mm, "end": v(-17.56, -13.07) * mm});
            skLineSegment(sketch, "E720", {"start": v(-17.56, -13.07) * mm, "end": v(-17.4, -13.03) * mm});
            skLineSegment(sketch, "E721", {"start": v(-17.4, -13.03) * mm, "end": v(-17.23, -12.98) * mm});
            skLineSegment(sketch, "E722", {"start": v(-17.23, -12.98) * mm, "end": v(-17.08, -12.93) * mm});
            skLineSegment(sketch, "E723", {"start": v(-17.08, -12.93) * mm, "end": v(-16.94, -12.89) * mm});
            skLineSegment(sketch, "E724", {"start": v(-16.94, -12.89) * mm, "end": v(-16.81, -12.84) * mm});
            skLineSegment(sketch, "E725", {"start": v(-16.81, -12.84) * mm, "end": v(-16.7, -12.8) * mm});
            skLineSegment(sketch, "E726", {"start": v(-16.7, -12.8) * mm, "end": v(-16.59, -12.75) * mm});
            skLineSegment(sketch, "E727", {"start": v(-16.59, -12.75) * mm, "end": v(-16.49, -12.7) * mm});
            skLineSegment(sketch, "E728", {"start": v(-16.49, -12.7) * mm, "end": v(-16.4, -12.66) * mm});
            skLineSegment(sketch, "E729", {"start": v(-16.4, -12.66) * mm, "end": v(-16.32, -12.62) * mm});
            skLineSegment(sketch, "E730", {"start": v(-16.32, -12.62) * mm, "end": v(-16.24, -12.58) * mm});
            skLineSegment(sketch, "E731", {"start": v(-16.24, -12.58) * mm, "end": v(-16.18, -12.55) * mm});
            skLineSegment(sketch, "E732", {"start": v(-16.18, -12.55) * mm, "end": v(-16.13, -12.52) * mm});
            skLineSegment(sketch, "E733", {"start": v(-16.13, -12.52) * mm, "end": v(-16.09, -12.5) * mm});
            skLineSegment(sketch, "E734", {"start": v(-16.09, -12.5) * mm, "end": v(-16.05, -12.47) * mm});
            skLineSegment(sketch, "E735", {"start": v(-16.05, -12.47) * mm, "end": v(-16.03, -12.45) * mm});
            skLineSegment(sketch, "E736", {"start": v(-16.03, -12.45) * mm, "end": v(-16, -12.44) * mm});
            skLineSegment(sketch, "E737", {"start": v(-16, -12.44) * mm, "end": v(-16, -12.43) * mm});
            skLineSegment(sketch, "E738", {"start": v(-16, -12.43) * mm, "end": v(-15.37, -11.95) * mm});
            skLineSegment(sketch, "E739", {"start": v(-15.37, -11.95) * mm, "end": v(-13.77, -13.77) * mm});
            skLineSegment(sketch, "E740", {"start": v(-13.77, -13.77) * mm, "end": v(-14.33, -14.33) * mm});
            skLineSegment(sketch, "E741", {"start": v(-14.33, -14.33) * mm, "end": v(-14.34, -14.34) * mm});
            skLineSegment(sketch, "E742", {"start": v(-14.34, -14.34) * mm, "end": v(-14.35, -14.35) * mm});
            skLineSegment(sketch, "E743", {"start": v(-14.35, -14.35) * mm, "end": v(-14.37, -14.38) * mm});
            skLineSegment(sketch, "E744", {"start": v(-14.37, -14.38) * mm, "end": v(-14.4, -14.4) * mm});
            skLineSegment(sketch, "E745", {"start": v(-14.4, -14.4) * mm, "end": v(-14.43, -14.45) * mm});
            skLineSegment(sketch, "E746", {"start": v(-14.43, -14.45) * mm, "end": v(-14.47, -14.5) * mm});
            skLineSegment(sketch, "E747", {"start": v(-14.47, -14.5) * mm, "end": v(-14.5, -14.55) * mm});
            skLineSegment(sketch, "E748", {"start": v(-14.5, -14.55) * mm, "end": v(-14.55, -14.62) * mm});
            skLineSegment(sketch, "E749", {"start": v(-14.55, -14.62) * mm, "end": v(-14.6, -14.7) * mm});
            skLineSegment(sketch, "E750", {"start": v(-14.6, -14.7) * mm, "end": v(-14.65, -14.78) * mm});
            skLineSegment(sketch, "E751", {"start": v(-14.65, -14.78) * mm, "end": v(-14.71, -14.87) * mm});
            skLineSegment(sketch, "E752", {"start": v(-14.71, -14.87) * mm, "end": v(-14.77, -14.98) * mm});
            skLineSegment(sketch, "E753", {"start": v(-14.77, -14.98) * mm, "end": v(-14.83, -15.09) * mm});
            skLineSegment(sketch, "E754", {"start": v(-14.83, -15.09) * mm, "end": v(-14.9, -15.21) * mm});
            skLineSegment(sketch, "E755", {"start": v(-14.9, -15.21) * mm, "end": v(-14.96, -15.34) * mm});
            skLineSegment(sketch, "E756", {"start": v(-14.96, -15.34) * mm, "end": v(-15.02, -15.49) * mm});
            skLineSegment(sketch, "E757", {"start": v(-15.02, -15.49) * mm, "end": v(-15.09, -15.64) * mm});
            skLineSegment(sketch, "E758", {"start": v(-15.09, -15.64) * mm, "end": v(-15.15, -15.8) * mm});
            skLineSegment(sketch, "E759", {"start": v(-15.15, -15.8) * mm, "end": v(-15.22, -15.98) * mm});
            skLineSegment(sketch, "E760", {"start": v(-15.22, -15.98) * mm, "end": v(-15.29, -16.16) * mm});
            skLineSegment(sketch, "E761", {"start": v(-15.29, -16.16) * mm, "end": v(-15.35, -16.36) * mm});
            skLineSegment(sketch, "E762", {"start": v(-15.35, -16.36) * mm, "end": v(-15.42, -16.56) * mm});
            skLineSegment(sketch, "E763", {"start": v(-15.42, -16.56) * mm, "end": v(-15.48, -16.78) * mm});
            skLineSegment(sketch, "E764", {"start": v(-15.48, -16.78) * mm, "end": v(-15.54, -17) * mm});
            skLineSegment(sketch, "E765", {"start": v(-15.54, -17) * mm, "end": v(-15.6, -17.24) * mm});
            skLineSegment(sketch, "E766", {"start": v(-15.6, -17.24) * mm, "end": v(-15.64, -17.49) * mm});
            skLineSegment(sketch, "E767", {"start": v(-15.64, -17.49) * mm, "end": v(-15.7, -17.75) * mm});
            skLineSegment(sketch, "E768", {"start": v(-15.7, -17.75) * mm, "end": v(-15.74, -18.02) * mm});
            skLineSegment(sketch, "E769", {"start": v(-15.74, -18.02) * mm, "end": v(-15.78, -18.3) * mm});
            skLineSegment(sketch, "E770", {"start": v(-15.78, -18.3) * mm, "end": v(-15.82, -18.59) * mm});
            skLineSegment(sketch, "E771", {"start": v(-15.82, -18.59) * mm, "end": v(-15.85, -18.89) * mm});
            skLineSegment(sketch, "E772", {"start": v(-15.85, -18.89) * mm, "end": v(-15.87, -19.2) * mm});
            skLineSegment(sketch, "E773", {"start": v(-15.87, -19.2) * mm, "end": v(-15.9, -19.52) * mm});
            skLineSegment(sketch, "E774", {"start": v(-15.9, -19.52) * mm, "end": v(-15.9, -19.85) * mm});
            skLineSegment(sketch, "E775", {"start": v(-15.9, -19.85) * mm, "end": v(-15.83, -20.09) * mm});
            skLineSegment(sketch, "E776", {"start": v(-15.83, -20.09) * mm, "end": v(-15.18, -20.59) * mm});
            skLineSegment(sketch, "E777", {"start": v(-15.18, -20.59) * mm, "end": v(-14.93, -20.6) * mm});
            skLineSegment(sketch, "E778", {"start": v(-14.93, -20.6) * mm, "end": v(-14.61, -20.5) * mm});
            skLineSegment(sketch, "E779", {"start": v(-14.61, -20.5) * mm, "end": v(-14.3, -20.4) * mm});
            skLineSegment(sketch, "E780", {"start": v(-14.3, -20.4) * mm, "end": v(-14.01, -20.28) * mm});
            skLineSegment(sketch, "E781", {"start": v(-14.01, -20.28) * mm, "end": v(-13.73, -20.18) * mm});
            skLineSegment(sketch, "E782", {"start": v(-13.73, -20.18) * mm, "end": v(-13.46, -20.06) * mm});
            skLineSegment(sketch, "E783", {"start": v(-13.46, -20.06) * mm, "end": v(-13.2, -19.95) * mm});
            skLineSegment(sketch, "E784", {"start": v(-13.2, -19.95) * mm, "end": v(-12.96, -19.83) * mm});
            skLineSegment(sketch, "E785", {"start": v(-12.96, -19.83) * mm, "end": v(-12.72, -19.72) * mm});
            skLineSegment(sketch, "E786", {"start": v(-12.72, -19.72) * mm, "end": v(-12.5, -19.6) * mm});
            skLineSegment(sketch, "E787", {"start": v(-12.5, -19.6) * mm, "end": v(-12.28, -19.48) * mm});
            skLineSegment(sketch, "E788", {"start": v(-12.28, -19.48) * mm, "end": v(-12.08, -19.37) * mm});
            skLineSegment(sketch, "E789", {"start": v(-12.08, -19.37) * mm, "end": v(-11.89, -19.25) * mm});
            skLineSegment(sketch, "E790", {"start": v(-11.89, -19.25) * mm, "end": v(-11.7, -19.14) * mm});
            skLineSegment(sketch, "E791", {"start": v(-11.7, -19.14) * mm, "end": v(-11.54, -19.02) * mm});
            skLineSegment(sketch, "E792", {"start": v(-11.54, -19.02) * mm, "end": v(-11.38, -18.9) * mm});
            skLineSegment(sketch, "E793", {"start": v(-11.38, -18.9) * mm, "end": v(-11.23, -18.8) * mm});
            skLineSegment(sketch, "E794", {"start": v(-11.23, -18.8) * mm, "end": v(-11.09, -18.7) * mm});
            skLineSegment(sketch, "E795", {"start": v(-11.09, -18.7) * mm, "end": v(-10.96, -18.59) * mm});
            skLineSegment(sketch, "E796", {"start": v(-10.96, -18.59) * mm, "end": v(-10.83, -18.49) * mm});
            skLineSegment(sketch, "E797", {"start": v(-10.83, -18.49) * mm, "end": v(-10.72, -18.39) * mm});
            skLineSegment(sketch, "E798", {"start": v(-10.72, -18.39) * mm, "end": v(-10.62, -18.3) * mm});
            skLineSegment(sketch, "E799", {"start": v(-10.62, -18.3) * mm, "end": v(-10.53, -18.2) * mm});
            skLineSegment(sketch, "E800", {"start": v(-10.53, -18.2) * mm, "end": v(-10.45, -18.12) * mm});
            skLineSegment(sketch, "E801", {"start": v(-10.45, -18.12) * mm, "end": v(-10.37, -18.04) * mm});
            skLineSegment(sketch, "E802", {"start": v(-10.37, -18.04) * mm, "end": v(-10.3, -17.97) * mm});
            skLineSegment(sketch, "E803", {"start": v(-10.3, -17.97) * mm, "end": v(-10.24, -17.9) * mm});
            skLineSegment(sketch, "E804", {"start": v(-10.24, -17.9) * mm, "end": v(-10.2, -17.84) * mm});
            skLineSegment(sketch, "E805", {"start": v(-10.2, -17.84) * mm, "end": v(-10.15, -17.79) * mm});
            skLineSegment(sketch, "E806", {"start": v(-10.15, -17.79) * mm, "end": v(-10.11, -17.74) * mm});
            skLineSegment(sketch, "E807", {"start": v(-10.11, -17.74) * mm, "end": v(-10.08, -17.7) * mm});
            skLineSegment(sketch, "E808", {"start": v(-10.08, -17.7) * mm, "end": v(-10.06, -17.67) * mm});
            skLineSegment(sketch, "E809", {"start": v(-10.06, -17.67) * mm, "end": v(-10.04, -17.64) * mm});
            skLineSegment(sketch, "E810", {"start": v(-10.04, -17.64) * mm, "end": v(-10.03, -17.62) * mm});
            skLineSegment(sketch, "E811", {"start": v(-10.03, -17.62) * mm, "end": v(-10.02, -17.6) * mm});
            skLineSegment(sketch, "E812", {"start": v(-10.02, -17.6) * mm, "end": v(-9.63, -16.92) * mm});
            skLineSegment(sketch, "E813", {"start": v(-9.63, -16.92) * mm, "end": v(-7.45, -17.99) * mm});
            skLineSegment(sketch, "E814", {"start": v(-7.45, -17.99) * mm, "end": v(-7.75, -18.72) * mm});
            skLineSegment(sketch, "E815", {"start": v(-7.75, -18.72) * mm, "end": v(-7.76, -18.73) * mm});
            skLineSegment(sketch, "E816", {"start": v(-7.76, -18.73) * mm, "end": v(-7.76, -18.75) * mm});
            skLineSegment(sketch, "E817", {"start": v(-7.76, -18.75) * mm, "end": v(-7.78, -18.78) * mm});
            skLineSegment(sketch, "E818", {"start": v(-7.78, -18.78) * mm, "end": v(-7.79, -18.82) * mm});
            skLineSegment(sketch, "E819", {"start": v(-7.79, -18.82) * mm, "end": v(-7.8, -18.87) * mm});
            skLineSegment(sketch, "E820", {"start": v(-7.8, -18.87) * mm, "end": v(-7.82, -18.93) * mm});
            skLineSegment(sketch, "E821", {"start": v(-7.82, -18.93) * mm, "end": v(-7.83, -19) * mm});
            skLineSegment(sketch, "E822", {"start": v(-7.83, -19) * mm, "end": v(-7.85, -19.08) * mm});
            skLineSegment(sketch, "E823", {"start": v(-7.85, -19.08) * mm, "end": v(-7.87, -19.16) * mm});
            skLineSegment(sketch, "E824", {"start": v(-7.87, -19.16) * mm, "end": v(-7.88, -19.26) * mm});
            skLineSegment(sketch, "E825", {"start": v(-7.88, -19.26) * mm, "end": v(-7.9, -19.37) * mm});
            skLineSegment(sketch, "E826", {"start": v(-7.9, -19.37) * mm, "end": v(-7.91, -19.49) * mm});
            skLineSegment(sketch, "E827", {"start": v(-7.91, -19.49) * mm, "end": v(-7.93, -19.61) * mm});
            skLineSegment(sketch, "E828", {"start": v(-7.93, -19.61) * mm, "end": v(-7.94, -19.75) * mm});
            skLineSegment(sketch, "E829", {"start": v(-7.94, -19.75) * mm, "end": v(-7.95, -19.9) * mm});
            skLineSegment(sketch, "E830", {"start": v(-7.95, -19.9) * mm, "end": v(-7.95, -20.06) * mm});
            skLineSegment(sketch, "E831", {"start": v(-7.95, -20.06) * mm, "end": v(-7.95, -20.22) * mm});
            skLineSegment(sketch, "E832", {"start": v(-7.95, -20.22) * mm, "end": v(-7.95, -20.4) * mm});
            skLineSegment(sketch, "E833", {"start": v(-7.95, -20.4) * mm, "end": v(-7.95, -20.59) * mm});
            skLineSegment(sketch, "E834", {"start": v(-7.95, -20.59) * mm, "end": v(-7.94, -20.78) * mm});
            skLineSegment(sketch, "E835", {"start": v(-7.94, -20.78) * mm, "end": v(-7.92, -20.99) * mm});
            skLineSegment(sketch, "E836", {"start": v(-7.92, -20.99) * mm, "end": v(-7.9, -21.2) * mm});
            skLineSegment(sketch, "E837", {"start": v(-7.9, -21.2) * mm, "end": v(-7.88, -21.42) * mm});
            skLineSegment(sketch, "E838", {"start": v(-7.88, -21.42) * mm, "end": v(-7.85, -21.66) * mm});
            skLineSegment(sketch, "E839", {"start": v(-7.85, -21.66) * mm, "end": v(-7.8, -21.9) * mm});
            skLineSegment(sketch, "E840", {"start": v(-7.8, -21.9) * mm, "end": v(-7.76, -22.15) * mm});
            skLineSegment(sketch, "E841", {"start": v(-7.76, -22.15) * mm, "end": v(-7.7, -22.4) * mm});
            skLineSegment(sketch, "E842", {"start": v(-7.7, -22.4) * mm, "end": v(-7.65, -22.67) * mm});
            skLineSegment(sketch, "E843", {"start": v(-7.65, -22.67) * mm, "end": v(-7.58, -22.94) * mm});
            skLineSegment(sketch, "E844", {"start": v(-7.58, -22.94) * mm, "end": v(-7.5, -23.22) * mm});
            skLineSegment(sketch, "E845", {"start": v(-7.5, -23.22) * mm, "end": v(-7.41, -23.51) * mm});
            skLineSegment(sketch, "E846", {"start": v(-7.41, -23.51) * mm, "end": v(-7.32, -23.81) * mm});
            skLineSegment(sketch, "E847", {"start": v(-7.32, -23.81) * mm, "end": v(-7.21, -24.11) * mm});
            skLineSegment(sketch, "E848", {"start": v(-7.21, -24.11) * mm, "end": v(-7.1, -24.42) * mm});
            skLineSegment(sketch, "E849", {"start": v(-7.1, -24.42) * mm, "end": v(-6.94, -24.62) * mm});
            skLineSegment(sketch, "E850", {"start": v(-6.94, -24.62) * mm, "end": v(-6.15, -24.83) * mm});
            skLineSegment(sketch, "E851", {"start": v(-6.15, -24.83) * mm, "end": v(-5.91, -24.74) * mm});
            skLineSegment(sketch, "E852", {"start": v(-5.91, -24.74) * mm, "end": v(-5.66, -24.53) * mm});
            skLineSegment(sketch, "E853", {"start": v(-5.66, -24.53) * mm, "end": v(-5.42, -24.31) * mm});
            skLineSegment(sketch, "E854", {"start": v(-5.42, -24.31) * mm, "end": v(-5.19, -24.1) * mm});
            skLineSegment(sketch, "E855", {"start": v(-5.19, -24.1) * mm, "end": v(-4.97, -23.9) * mm});
            skLineSegment(sketch, "E856", {"start": v(-4.97, -23.9) * mm, "end": v(-4.76, -23.69) * mm});
            skLineSegment(sketch, "E857", {"start": v(-4.76, -23.69) * mm, "end": v(-4.57, -23.48) * mm});
            skLineSegment(sketch, "E858", {"start": v(-4.57, -23.48) * mm, "end": v(-4.38, -23.28) * mm});
            skLineSegment(sketch, "E859", {"start": v(-4.38, -23.28) * mm, "end": v(-4.2, -23.09) * mm});
            skLineSegment(sketch, "E860", {"start": v(-4.2, -23.09) * mm, "end": v(-4.04, -22.9) * mm});
            skLineSegment(sketch, "E861", {"start": v(-4.04, -22.9) * mm, "end": v(-3.9, -22.7) * mm});
            skLineSegment(sketch, "E862", {"start": v(-3.9, -22.7) * mm, "end": v(-3.75, -22.52) * mm});
            skLineSegment(sketch, "E863", {"start": v(-3.75, -22.52) * mm, "end": v(-3.62, -22.33) * mm});
            skLineSegment(sketch, "E864", {"start": v(-3.62, -22.33) * mm, "end": v(-3.5, -22.16) * mm});
            skLineSegment(sketch, "E865", {"start": v(-3.5, -22.16) * mm, "end": v(-3.38, -21.99) * mm});
            skLineSegment(sketch, "E866", {"start": v(-3.38, -21.99) * mm, "end": v(-3.27, -21.82) * mm});
            skLineSegment(sketch, "E867", {"start": v(-3.27, -21.82) * mm, "end": v(-3.18, -21.66) * mm});
            skLineSegment(sketch, "E868", {"start": v(-3.18, -21.66) * mm, "end": v(-3.09, -21.51) * mm});
            skLineSegment(sketch, "E869", {"start": v(-3.09, -21.51) * mm, "end": v(-3, -21.36) * mm});
            skLineSegment(sketch, "E870", {"start": v(-3, -21.36) * mm, "end": v(-2.94, -21.23) * mm});
            skLineSegment(sketch, "E871", {"start": v(-2.94, -21.23) * mm, "end": v(-2.87, -21.1) * mm});
            skLineSegment(sketch, "E872", {"start": v(-2.87, -21.1) * mm, "end": v(-2.81, -20.97) * mm});
            skLineSegment(sketch, "E873", {"start": v(-2.81, -20.97) * mm, "end": v(-2.76, -20.85) * mm});
            skLineSegment(sketch, "E874", {"start": v(-2.76, -20.85) * mm, "end": v(-2.71, -20.74) * mm});
            skLineSegment(sketch, "E875", {"start": v(-2.71, -20.74) * mm, "end": v(-2.67, -20.64) * mm});
            skLineSegment(sketch, "E876", {"start": v(-2.67, -20.64) * mm, "end": v(-2.64, -20.55) * mm});
            skLineSegment(sketch, "E877", {"start": v(-2.64, -20.55) * mm, "end": v(-2.61, -20.46) * mm});
            skLineSegment(sketch, "E878", {"start": v(-2.61, -20.46) * mm, "end": v(-2.59, -20.39) * mm});
            skLineSegment(sketch, "E879", {"start": v(-2.59, -20.39) * mm, "end": v(-2.57, -20.32) * mm});
            skLineSegment(sketch, "E880", {"start": v(-2.57, -20.32) * mm, "end": v(-2.55, -20.26) * mm});
            skLineSegment(sketch, "E881", {"start": v(-2.55, -20.26) * mm, "end": v(-2.54, -20.2) * mm});
            skLineSegment(sketch, "E882", {"start": v(-2.54, -20.2) * mm, "end": v(-2.53, -20.17) * mm});
            skLineSegment(sketch, "E883", {"start": v(-2.53, -20.17) * mm, "end": v(-2.53, -20.14) * mm});
            skLineSegment(sketch, "E884", {"start": v(-2.53, -20.14) * mm, "end": v(-2.52, -20.12) * mm});
            skLineSegment(sketch, "E885", {"start": v(-2.52, -20.12) * mm, "end": v(-2.52, -20.1) * mm});
            skLineSegment(sketch, "E886", {"start": v(-2.52, -20.1) * mm, "end": v(-2.42, -19.32) * mm});
            skLineSegment(sketch, "E887", {"start": v(-2.42, -19.32) * mm, "end": v(0, -19.47) * mm});
            skLineSegment(sketch, "E888", {"start": v(0, -19.47) * mm, "end": v(0, -20.26) * mm});
            skLineSegment(sketch, "E889", {"start": v(0, -20.26) * mm, "end": v(0, -20.27) * mm});
            skLineSegment(sketch, "E890", {"start": v(0, -20.27) * mm, "end": v(0, -20.3) * mm});
            skLineSegment(sketch, "E891", {"start": v(0, -20.3) * mm, "end": v(0, -20.33) * mm});
            skLineSegment(sketch, "E892", {"start": v(0, -20.33) * mm, "end": v(0, -20.37) * mm});
            skLineSegment(sketch, "E893", {"start": v(0, -20.37) * mm, "end": v(0.01, -20.42) * mm});
            skLineSegment(sketch, "E894", {"start": v(0.01, -20.42) * mm, "end": v(0.02, -20.48) * mm});
            skLineSegment(sketch, "E895", {"start": v(0.02, -20.48) * mm, "end": v(0.03, -20.55) * mm});
            skLineSegment(sketch, "E896", {"start": v(0.03, -20.55) * mm, "end": v(0.05, -20.63) * mm});
            skLineSegment(sketch, "E897", {"start": v(0.05, -20.63) * mm, "end": v(0.07, -20.72) * mm});
            skLineSegment(sketch, "E898", {"start": v(0.07, -20.72) * mm, "end": v(0.09, -20.81) * mm});
            skLineSegment(sketch, "E899", {"start": v(0.09, -20.81) * mm, "end": v(0.11, -20.92) * mm});
            skLineSegment(sketch, "E900", {"start": v(0.11, -20.92) * mm, "end": v(0.15, -21.03) * mm});
            skLineSegment(sketch, "E901", {"start": v(0.15, -21.03) * mm, "end": v(0.18, -21.15) * mm});
            skLineSegment(sketch, "E902", {"start": v(0.18, -21.15) * mm, "end": v(0.22, -21.29) * mm});
            skLineSegment(sketch, "E903", {"start": v(0.22, -21.29) * mm, "end": v(0.27, -21.43) * mm});
            skLineSegment(sketch, "E904", {"start": v(0.27, -21.43) * mm, "end": v(0.33, -21.57) * mm});
            skLineSegment(sketch, "E905", {"start": v(0.33, -21.57) * mm, "end": v(0.39, -21.73) * mm});
            skLineSegment(sketch, "E906", {"start": v(0.39, -21.73) * mm, "end": v(0.46, -21.9) * mm});
            skLineSegment(sketch, "E907", {"start": v(0.46, -21.9) * mm, "end": v(0.53, -22.06) * mm});
            skLineSegment(sketch, "E908", {"start": v(0.53, -22.06) * mm, "end": v(0.62, -22.24) * mm});
            skLineSegment(sketch, "E909", {"start": v(0.62, -22.24) * mm, "end": v(0.71, -22.42) * mm});
            skLineSegment(sketch, "E910", {"start": v(0.71, -22.42) * mm, "end": v(0.81, -22.61) * mm});
            skLineSegment(sketch, "E911", {"start": v(0.81, -22.61) * mm, "end": v(0.92, -22.8) * mm});
            skLineSegment(sketch, "E912", {"start": v(0.92, -22.8) * mm, "end": v(1.04, -23) * mm});
            skLineSegment(sketch, "E913", {"start": v(1.04, -23) * mm, "end": v(1.17, -23.22) * mm});
            skLineSegment(sketch, "E914", {"start": v(1.17, -23.22) * mm, "end": v(1.3, -23.43) * mm});
            skLineSegment(sketch, "E915", {"start": v(1.3, -23.43) * mm, "end": v(1.45, -23.65) * mm});
            skLineSegment(sketch, "E916", {"start": v(1.45, -23.65) * mm, "end": v(1.6, -23.87) * mm});
            skLineSegment(sketch, "E917", {"start": v(1.6, -23.87) * mm, "end": v(1.78, -24.1) * mm});
            skLineSegment(sketch, "E918", {"start": v(1.78, -24.1) * mm, "end": v(1.96, -24.33) * mm});
            skLineSegment(sketch, "E919", {"start": v(1.96, -24.33) * mm, "end": v(2.15, -24.56) * mm});
            skLineSegment(sketch, "E920", {"start": v(2.15, -24.56) * mm, "end": v(2.35, -24.8) * mm});
            skLineSegment(sketch, "E921", {"start": v(2.35, -24.8) * mm, "end": v(2.56, -25.04) * mm});
            skLineSegment(sketch, "E922", {"start": v(2.56, -25.04) * mm, "end": v(2.79, -25.28) * mm});
            skLineSegment(sketch, "E923", {"start": v(2.79, -25.28) * mm, "end": v(3.01, -25.4) * mm});
            skLineSegment(sketch, "E924", {"start": v(3.01, -25.4) * mm, "end": v(3.82, -25.3) * mm});
            skLineSegment(sketch, "E925", {"start": v(3.82, -25.3) * mm, "end": v(4, -25.12) * mm});
            skLineSegment(sketch, "E926", {"start": v(4, -25.12) * mm, "end": v(4.16, -24.82) * mm});
            skLineSegment(sketch, "E927", {"start": v(4.16, -24.82) * mm, "end": v(4.3, -24.54) * mm});
            skLineSegment(sketch, "E928", {"start": v(4.3, -24.54) * mm, "end": v(4.43, -24.25) * mm});
            skLineSegment(sketch, "E929", {"start": v(4.43, -24.25) * mm, "end": v(4.55, -23.98) * mm});
            skLineSegment(sketch, "E930", {"start": v(4.55, -23.98) * mm, "end": v(4.67, -23.7) * mm});
            skLineSegment(sketch, "E931", {"start": v(4.67, -23.7) * mm, "end": v(4.77, -23.44) * mm});
            skLineSegment(sketch, "E932", {"start": v(4.77, -23.44) * mm, "end": v(4.86, -23.19) * mm});
            skLineSegment(sketch, "E933", {"start": v(4.86, -23.19) * mm, "end": v(4.95, -22.94) * mm});
            skLineSegment(sketch, "E934", {"start": v(4.95, -22.94) * mm, "end": v(5.02, -22.7) * mm});
            skLineSegment(sketch, "E935", {"start": v(5.02, -22.7) * mm, "end": v(5.1, -22.46) * mm});
            skLineSegment(sketch, "E936", {"start": v(5.1, -22.46) * mm, "end": v(5.15, -22.24) * mm});
            skLineSegment(sketch, "E937", {"start": v(5.15, -22.24) * mm, "end": v(5.2, -22.02) * mm});
            skLineSegment(sketch, "E938", {"start": v(5.2, -22.02) * mm, "end": v(5.25, -21.8) * mm});
            skLineSegment(sketch, "E939", {"start": v(5.25, -21.8) * mm, "end": v(5.3, -21.6) * mm});
            skLineSegment(sketch, "E940", {"start": v(5.3, -21.6) * mm, "end": v(5.33, -21.41) * mm});
            skLineSegment(sketch, "E941", {"start": v(5.33, -21.41) * mm, "end": v(5.36, -21.23) * mm});
            skLineSegment(sketch, "E942", {"start": v(5.36, -21.23) * mm, "end": v(5.38, -21.06) * mm});
            skLineSegment(sketch, "E943", {"start": v(5.38, -21.06) * mm, "end": v(5.4, -20.89) * mm});
            skLineSegment(sketch, "E944", {"start": v(5.4, -20.89) * mm, "end": v(5.41, -20.73) * mm});
            skLineSegment(sketch, "E945", {"start": v(5.41, -20.73) * mm, "end": v(5.42, -20.59) * mm});
            skLineSegment(sketch, "E946", {"start": v(5.42, -20.59) * mm, "end": v(5.43, -20.45) * mm});
            skLineSegment(sketch, "E947", {"start": v(5.43, -20.45) * mm, "end": v(5.43, -20.32) * mm});
            skLineSegment(sketch, "E948", {"start": v(5.43, -20.32) * mm, "end": v(5.43, -20.2) * mm});
            skLineSegment(sketch, "E949", {"start": v(5.43, -20.2) * mm, "end": v(5.43, -20.1) * mm});
            skLineSegment(sketch, "E950", {"start": v(5.43, -20.1) * mm, "end": v(5.42, -20) * mm});
            skLineSegment(sketch, "E951", {"start": v(5.42, -20) * mm, "end": v(5.42, -19.9) * mm});
            skLineSegment(sketch, "E952", {"start": v(5.42, -19.9) * mm, "end": v(5.4, -19.82) * mm});
            skLineSegment(sketch, "E953", {"start": v(5.4, -19.82) * mm, "end": v(5.4, -19.75) * mm});
            skLineSegment(sketch, "E954", {"start": v(5.4, -19.75) * mm, "end": v(5.4, -19.7) * mm});
            skLineSegment(sketch, "E955", {"start": v(5.4, -19.7) * mm, "end": v(5.39, -19.64) * mm});
            skLineSegment(sketch, "E956", {"start": v(5.39, -19.64) * mm, "end": v(5.38, -19.6) * mm});
            skLineSegment(sketch, "E957", {"start": v(5.38, -19.6) * mm, "end": v(5.37, -19.57) * mm});
            skLineSegment(sketch, "E958", {"start": v(5.37, -19.57) * mm, "end": v(5.37, -19.55) * mm});
            skLineSegment(sketch, "E959", {"start": v(5.37, -19.55) * mm, "end": v(5.37, -19.54) * mm});
            skLineSegment(sketch, "E960", {"start": v(5.37, -19.54) * mm, "end": v(5.16, -18.77) * mm});
            skLineSegment(sketch, "E961", {"start": v(5.16, -18.77) * mm, "end": v(7.45, -17.99) * mm});
            skLineSegment(sketch, "E962", {"start": v(7.45, -17.99) * mm, "end": v(7.75, -18.72) * mm});
            skLineSegment(sketch, "E963", {"start": v(7.75, -18.72) * mm, "end": v(7.76, -18.73) * mm});
            skLineSegment(sketch, "E964", {"start": v(7.76, -18.73) * mm, "end": v(7.77, -18.75) * mm});
            skLineSegment(sketch, "E965", {"start": v(7.77, -18.75) * mm, "end": v(7.78, -18.78) * mm});
            skLineSegment(sketch, "E966", {"start": v(7.78, -18.78) * mm, "end": v(7.8, -18.81) * mm});
            skLineSegment(sketch, "E967", {"start": v(7.8, -18.81) * mm, "end": v(7.83, -18.86) * mm});
            skLineSegment(sketch, "E968", {"start": v(7.83, -18.86) * mm, "end": v(7.86, -18.91) * mm});
            skLineSegment(sketch, "E969", {"start": v(7.86, -18.91) * mm, "end": v(7.9, -18.97) * mm});
            skLineSegment(sketch, "E970", {"start": v(7.9, -18.97) * mm, "end": v(7.94, -19.04) * mm});
            skLineSegment(sketch, "E971", {"start": v(7.94, -19.04) * mm, "end": v(7.99, -19.11) * mm});
            skLineSegment(sketch, "E972", {"start": v(7.99, -19.11) * mm, "end": v(8.05, -19.2) * mm});
            skLineSegment(sketch, "E973", {"start": v(8.05, -19.2) * mm, "end": v(8.11, -19.28) * mm});
            skLineSegment(sketch, "E974", {"start": v(8.11, -19.28) * mm, "end": v(8.18, -19.38) * mm});
            skLineSegment(sketch, "E975", {"start": v(8.18, -19.38) * mm, "end": v(8.26, -19.47) * mm});
            skLineSegment(sketch, "E976", {"start": v(8.26, -19.47) * mm, "end": v(8.35, -19.58) * mm});
            skLineSegment(sketch, "E977", {"start": v(8.35, -19.58) * mm, "end": v(8.45, -19.7) * mm});
            skLineSegment(sketch, "E978", {"start": v(8.45, -19.7) * mm, "end": v(8.56, -19.8) * mm});
            skLineSegment(sketch, "E979", {"start": v(8.56, -19.8) * mm, "end": v(8.68, -19.93) * mm});
            skLineSegment(sketch, "E980", {"start": v(8.68, -19.93) * mm, "end": v(8.8, -20.05) * mm});
            skLineSegment(sketch, "E981", {"start": v(8.8, -20.05) * mm, "end": v(8.94, -20.18) * mm});
            skLineSegment(sketch, "E982", {"start": v(8.94, -20.18) * mm, "end": v(9.08, -20.3) * mm});
            skLineSegment(sketch, "E983", {"start": v(9.08, -20.3) * mm, "end": v(9.24, -20.44) * mm});
            skLineSegment(sketch, "E984", {"start": v(9.24, -20.44) * mm, "end": v(9.4, -20.58) * mm});
            skLineSegment(sketch, "E985", {"start": v(9.4, -20.58) * mm, "end": v(9.58, -20.72) * mm});
            skLineSegment(sketch, "E986", {"start": v(9.58, -20.72) * mm, "end": v(9.76, -20.86) * mm});
            skLineSegment(sketch, "E987", {"start": v(9.76, -20.86) * mm, "end": v(9.96, -21) * mm});
            skLineSegment(sketch, "E988", {"start": v(9.96, -21) * mm, "end": v(10.17, -21.15) * mm});
            skLineSegment(sketch, "E989", {"start": v(10.17, -21.15) * mm, "end": v(10.4, -21.3) * mm});
            skLineSegment(sketch, "E990", {"start": v(10.4, -21.3) * mm, "end": v(10.62, -21.44) * mm});
            skLineSegment(sketch, "E991", {"start": v(10.62, -21.44) * mm, "end": v(10.86, -21.58) * mm});
            skLineSegment(sketch, "E992", {"start": v(10.86, -21.58) * mm, "end": v(11.12, -21.73) * mm});
            skLineSegment(sketch, "E993", {"start": v(11.12, -21.73) * mm, "end": v(11.38, -21.87) * mm});
            skLineSegment(sketch, "E994", {"start": v(11.38, -21.87) * mm, "end": v(11.66, -22.01) * mm});
            skLineSegment(sketch, "E995", {"start": v(11.66, -22.01) * mm, "end": v(11.95, -22.15) * mm});
            skLineSegment(sketch, "E996", {"start": v(11.95, -22.15) * mm, "end": v(12.25, -22.29) * mm});
            skLineSegment(sketch, "E997", {"start": v(12.25, -22.29) * mm, "end": v(12.5, -22.31) * mm});
            skLineSegment(sketch, "E998", {"start": v(12.5, -22.31) * mm, "end": v(13.21, -21.9) * mm});
            skLineSegment(sketch, "E999", {"start": v(13.21, -21.9) * mm, "end": v(13.31, -21.67) * mm});
            skLineSegment(sketch, "E1000", {"start": v(13.31, -21.67) * mm, "end": v(13.34, -21.34) * mm});
            skLineSegment(sketch, "E1001", {"start": v(13.34, -21.34) * mm, "end": v(13.36, -21.02) * mm});
            skLineSegment(sketch, "E1002", {"start": v(13.36, -21.02) * mm, "end": v(13.38, -20.71) * mm});
            skLineSegment(sketch, "E1003", {"start": v(13.38, -20.71) * mm, "end": v(13.38, -20.4) * mm});
            skLineSegment(sketch, "E1004", {"start": v(13.38, -20.4) * mm, "end": v(13.38, -20.12) * mm});
            skLineSegment(sketch, "E1005", {"start": v(13.38, -20.12) * mm, "end": v(13.38, -19.83) * mm});
            skLineSegment(sketch, "E1006", {"start": v(13.38, -19.83) * mm, "end": v(13.37, -19.56) * mm});
            skLineSegment(sketch, "E1007", {"start": v(13.37, -19.56) * mm, "end": v(13.35, -19.3) * mm});
            skLineSegment(sketch, "E1008", {"start": v(13.35, -19.3) * mm, "end": v(13.33, -19.05) * mm});
            skLineSegment(sketch, "E1009", {"start": v(13.33, -19.05) * mm, "end": v(13.3, -18.8) * mm});
            skLineSegment(sketch, "E1010", {"start": v(13.3, -18.8) * mm, "end": v(13.27, -18.57) * mm});
            skLineSegment(sketch, "E1011", {"start": v(13.27, -18.57) * mm, "end": v(13.24, -18.35) * mm});
            skLineSegment(sketch, "E1012", {"start": v(13.24, -18.35) * mm, "end": v(13.2, -18.14) * mm});
            skLineSegment(sketch, "E1013", {"start": v(13.2, -18.14) * mm, "end": v(13.16, -17.94) * mm});
            skLineSegment(sketch, "E1014", {"start": v(13.16, -17.94) * mm, "end": v(13.12, -17.75) * mm});
            skLineSegment(sketch, "E1015", {"start": v(13.12, -17.75) * mm, "end": v(13.07, -17.56) * mm});
            skLineSegment(sketch, "E1016", {"start": v(13.07, -17.56) * mm, "end": v(13.03, -17.4) * mm});
            skLineSegment(sketch, "E1017", {"start": v(13.03, -17.4) * mm, "end": v(12.98, -17.23) * mm});
            skLineSegment(sketch, "E1018", {"start": v(12.98, -17.23) * mm, "end": v(12.93, -17.08) * mm});
            skLineSegment(sketch, "E1019", {"start": v(12.93, -17.08) * mm, "end": v(12.89, -16.94) * mm});
            skLineSegment(sketch, "E1020", {"start": v(12.89, -16.94) * mm, "end": v(12.84, -16.81) * mm});
            skLineSegment(sketch, "E1021", {"start": v(12.84, -16.81) * mm, "end": v(12.8, -16.7) * mm});
            skLineSegment(sketch, "E1022", {"start": v(12.8, -16.7) * mm, "end": v(12.75, -16.59) * mm});
            skLineSegment(sketch, "E1023", {"start": v(12.75, -16.59) * mm, "end": v(12.7, -16.49) * mm});
            skLineSegment(sketch, "E1024", {"start": v(12.7, -16.49) * mm, "end": v(12.66, -16.4) * mm});
            skLineSegment(sketch, "E1025", {"start": v(12.66, -16.4) * mm, "end": v(12.62, -16.32) * mm});
            skLineSegment(sketch, "E1026", {"start": v(12.62, -16.32) * mm, "end": v(12.58, -16.24) * mm});
            skLineSegment(sketch, "E1027", {"start": v(12.58, -16.24) * mm, "end": v(12.55, -16.18) * mm});
            skLineSegment(sketch, "E1028", {"start": v(12.55, -16.18) * mm, "end": v(12.52, -16.13) * mm});
            skLineSegment(sketch, "E1029", {"start": v(12.52, -16.13) * mm, "end": v(12.5, -16.09) * mm});
            skLineSegment(sketch, "E1030", {"start": v(12.5, -16.09) * mm, "end": v(12.47, -16.05) * mm});
            skLineSegment(sketch, "E1031", {"start": v(12.47, -16.05) * mm, "end": v(12.45, -16.03) * mm});
            skLineSegment(sketch, "E1032", {"start": v(12.45, -16.03) * mm, "end": v(12.44, -16) * mm});
            skLineSegment(sketch, "E1033", {"start": v(12.44, -16) * mm, "end": v(12.43, -16) * mm});
            skLineSegment(sketch, "E1034", {"start": v(12.43, -16) * mm, "end": v(11.95, -15.37) * mm});
            skLineSegment(sketch, "E1035", {"start": v(11.95, -15.37) * mm, "end": v(13.77, -13.77) * mm});
            skLineSegment(sketch, "E1036", {"start": v(13.77, -13.77) * mm, "end": v(14.33, -14.33) * mm});
            skLineSegment(sketch, "E1037", {"start": v(14.33, -14.33) * mm, "end": v(14.34, -14.34) * mm});
            skLineSegment(sketch, "E1038", {"start": v(14.34, -14.34) * mm, "end": v(14.35, -14.35) * mm});
            skLineSegment(sketch, "E1039", {"start": v(14.35, -14.35) * mm, "end": v(14.38, -14.37) * mm});
            skLineSegment(sketch, "E1040", {"start": v(14.38, -14.37) * mm, "end": v(14.4, -14.4) * mm});
            skLineSegment(sketch, "E1041", {"start": v(14.4, -14.4) * mm, "end": v(14.45, -14.43) * mm});
            skLineSegment(sketch, "E1042", {"start": v(14.45, -14.43) * mm, "end": v(14.5, -14.47) * mm});
            skLineSegment(sketch, "E1043", {"start": v(14.5, -14.47) * mm, "end": v(14.55, -14.5) * mm});
            skLineSegment(sketch, "E1044", {"start": v(14.55, -14.5) * mm, "end": v(14.62, -14.55) * mm});
            skLineSegment(sketch, "E1045", {"start": v(14.62, -14.55) * mm, "end": v(14.7, -14.6) * mm});
            skLineSegment(sketch, "E1046", {"start": v(14.7, -14.6) * mm, "end": v(14.78, -14.65) * mm});
            skLineSegment(sketch, "E1047", {"start": v(14.78, -14.65) * mm, "end": v(14.87, -14.71) * mm});
            skLineSegment(sketch, "E1048", {"start": v(14.87, -14.71) * mm, "end": v(14.98, -14.77) * mm});
            skLineSegment(sketch, "E1049", {"start": v(14.98, -14.77) * mm, "end": v(15.09, -14.83) * mm});
            skLineSegment(sketch, "E1050", {"start": v(15.09, -14.83) * mm, "end": v(15.21, -14.9) * mm});
            skLineSegment(sketch, "E1051", {"start": v(15.21, -14.9) * mm, "end": v(15.34, -14.96) * mm});
            skLineSegment(sketch, "E1052", {"start": v(15.34, -14.96) * mm, "end": v(15.49, -15.02) * mm});
            skLineSegment(sketch, "E1053", {"start": v(15.49, -15.02) * mm, "end": v(15.64, -15.09) * mm});
            skLineSegment(sketch, "E1054", {"start": v(15.64, -15.09) * mm, "end": v(15.8, -15.15) * mm});
            skLineSegment(sketch, "E1055", {"start": v(15.8, -15.15) * mm, "end": v(15.98, -15.22) * mm});
            skLineSegment(sketch, "E1056", {"start": v(15.98, -15.22) * mm, "end": v(16.16, -15.29) * mm});
            skLineSegment(sketch, "E1057", {"start": v(16.16, -15.29) * mm, "end": v(16.36, -15.35) * mm});
            skLineSegment(sketch, "E1058", {"start": v(16.36, -15.35) * mm, "end": v(16.56, -15.42) * mm});
            skLineSegment(sketch, "E1059", {"start": v(16.56, -15.42) * mm, "end": v(16.78, -15.48) * mm});
            skLineSegment(sketch, "E1060", {"start": v(16.78, -15.48) * mm, "end": v(17, -15.54) * mm});
            skLineSegment(sketch, "E1061", {"start": v(17, -15.54) * mm, "end": v(17.24, -15.6) * mm});
            skLineSegment(sketch, "E1062", {"start": v(17.24, -15.6) * mm, "end": v(17.49, -15.64) * mm});
            skLineSegment(sketch, "E1063", {"start": v(17.49, -15.64) * mm, "end": v(17.75, -15.7) * mm});
            skLineSegment(sketch, "E1064", {"start": v(17.75, -15.7) * mm, "end": v(18.02, -15.74) * mm});
            skLineSegment(sketch, "E1065", {"start": v(18.02, -15.74) * mm, "end": v(18.3, -15.78) * mm});
            skLineSegment(sketch, "E1066", {"start": v(18.3, -15.78) * mm, "end": v(18.59, -15.82) * mm});
            skLineSegment(sketch, "E1067", {"start": v(18.59, -15.82) * mm, "end": v(18.89, -15.85) * mm});
            skLineSegment(sketch, "E1068", {"start": v(18.89, -15.85) * mm, "end": v(19.2, -15.87) * mm});
            skLineSegment(sketch, "E1069", {"start": v(19.2, -15.87) * mm, "end": v(19.52, -15.9) * mm});
            skLineSegment(sketch, "E1070", {"start": v(19.52, -15.9) * mm, "end": v(19.85, -15.9) * mm});
            skLineSegment(sketch, "E1071", {"start": v(19.85, -15.9) * mm, "end": v(20.09, -15.83) * mm});
            skLineSegment(sketch, "E1072", {"start": v(20.09, -15.83) * mm, "end": v(20.59, -15.18) * mm});
            skLineSegment(sketch, "E1073", {"start": v(20.59, -15.18) * mm, "end": v(20.6, -14.93) * mm});
            skLineSegment(sketch, "E1074", {"start": v(20.6, -14.93) * mm, "end": v(20.5, -14.61) * mm});
            skLineSegment(sketch, "E1075", {"start": v(20.5, -14.61) * mm, "end": v(20.4, -14.3) * mm});
            skLineSegment(sketch, "E1076", {"start": v(20.4, -14.3) * mm, "end": v(20.28, -14.01) * mm});
            skLineSegment(sketch, "E1077", {"start": v(20.28, -14.01) * mm, "end": v(20.18, -13.73) * mm});
            skLineSegment(sketch, "E1078", {"start": v(20.18, -13.73) * mm, "end": v(20.06, -13.46) * mm});
            skLineSegment(sketch, "E1079", {"start": v(20.06, -13.46) * mm, "end": v(19.95, -13.2) * mm});
            skLineSegment(sketch, "E1080", {"start": v(19.95, -13.2) * mm, "end": v(19.83, -12.96) * mm});
            skLineSegment(sketch, "E1081", {"start": v(19.83, -12.96) * mm, "end": v(19.72, -12.72) * mm});
            skLineSegment(sketch, "E1082", {"start": v(19.72, -12.72) * mm, "end": v(19.6, -12.5) * mm});
            skLineSegment(sketch, "E1083", {"start": v(19.6, -12.5) * mm, "end": v(19.48, -12.28) * mm});
            skLineSegment(sketch, "E1084", {"start": v(19.48, -12.28) * mm, "end": v(19.37, -12.08) * mm});
            skLineSegment(sketch, "E1085", {"start": v(19.37, -12.08) * mm, "end": v(19.25, -11.89) * mm});
            skLineSegment(sketch, "E1086", {"start": v(19.25, -11.89) * mm, "end": v(19.14, -11.7) * mm});
            skLineSegment(sketch, "E1087", {"start": v(19.14, -11.7) * mm, "end": v(19.02, -11.54) * mm});
            skLineSegment(sketch, "E1088", {"start": v(19.02, -11.54) * mm, "end": v(18.9, -11.38) * mm});
            skLineSegment(sketch, "E1089", {"start": v(18.9, -11.38) * mm, "end": v(18.8, -11.23) * mm});
            skLineSegment(sketch, "E1090", {"start": v(18.8, -11.23) * mm, "end": v(18.7, -11.09) * mm});
            skLineSegment(sketch, "E1091", {"start": v(18.7, -11.09) * mm, "end": v(18.59, -10.96) * mm});
            skLineSegment(sketch, "E1092", {"start": v(18.59, -10.96) * mm, "end": v(18.49, -10.83) * mm});
            skLineSegment(sketch, "E1093", {"start": v(18.49, -10.83) * mm, "end": v(18.39, -10.72) * mm});
            skLineSegment(sketch, "E1094", {"start": v(18.39, -10.72) * mm, "end": v(18.3, -10.62) * mm});
            skLineSegment(sketch, "E1095", {"start": v(18.3, -10.62) * mm, "end": v(18.2, -10.53) * mm});
            skLineSegment(sketch, "E1096", {"start": v(18.2, -10.53) * mm, "end": v(18.12, -10.45) * mm});
            skLineSegment(sketch, "E1097", {"start": v(18.12, -10.45) * mm, "end": v(18.04, -10.37) * mm});
            skLineSegment(sketch, "E1098", {"start": v(18.04, -10.37) * mm, "end": v(17.97, -10.3) * mm});
            skLineSegment(sketch, "E1099", {"start": v(17.97, -10.3) * mm, "end": v(17.9, -10.24) * mm});
            skLineSegment(sketch, "E1100", {"start": v(17.9, -10.24) * mm, "end": v(17.84, -10.2) * mm});
            skLineSegment(sketch, "E1101", {"start": v(17.84, -10.2) * mm, "end": v(17.79, -10.15) * mm});
            skLineSegment(sketch, "E1102", {"start": v(17.79, -10.15) * mm, "end": v(17.74, -10.11) * mm});
            skLineSegment(sketch, "E1103", {"start": v(17.74, -10.11) * mm, "end": v(17.7, -10.08) * mm});
            skLineSegment(sketch, "E1104", {"start": v(17.7, -10.08) * mm, "end": v(17.67, -10.06) * mm});
            skLineSegment(sketch, "E1105", {"start": v(17.67, -10.06) * mm, "end": v(17.64, -10.04) * mm});
            skLineSegment(sketch, "E1106", {"start": v(17.64, -10.04) * mm, "end": v(17.62, -10.03) * mm});
            skLineSegment(sketch, "E1107", {"start": v(17.62, -10.03) * mm, "end": v(17.6, -10.02) * mm});
            skLineSegment(sketch, "E1108", {"start": v(17.6, -10.02) * mm, "end": v(16.92, -9.63) * mm});
            skLineSegment(sketch, "E1109", {"start": v(16.92, -9.63) * mm, "end": v(17.99, -7.45) * mm});
            skLineSegment(sketch, "E1110", {"start": v(17.99, -7.45) * mm, "end": v(18.72, -7.75) * mm});
            skLineSegment(sketch, "E1111", {"start": v(18.72, -7.75) * mm, "end": v(18.73, -7.76) * mm});
            skLineSegment(sketch, "E1112", {"start": v(18.73, -7.76) * mm, "end": v(18.75, -7.76) * mm});
            skLineSegment(sketch, "E1113", {"start": v(18.75, -7.76) * mm, "end": v(18.78, -7.78) * mm});
            skLineSegment(sketch, "E1114", {"start": v(18.78, -7.78) * mm, "end": v(18.82, -7.79) * mm});
            skLineSegment(sketch, "E1115", {"start": v(18.82, -7.79) * mm, "end": v(18.87, -7.8) * mm});
            skLineSegment(sketch, "E1116", {"start": v(18.87, -7.8) * mm, "end": v(18.93, -7.82) * mm});
            skLineSegment(sketch, "E1117", {"start": v(18.93, -7.82) * mm, "end": v(19, -7.83) * mm});
            skLineSegment(sketch, "E1118", {"start": v(19, -7.83) * mm, "end": v(19.08, -7.85) * mm});
            skLineSegment(sketch, "E1119", {"start": v(19.08, -7.85) * mm, "end": v(19.16, -7.87) * mm});
            skLineSegment(sketch, "E1120", {"start": v(19.16, -7.87) * mm, "end": v(19.26, -7.88) * mm});
            skLineSegment(sketch, "E1121", {"start": v(19.26, -7.88) * mm, "end": v(19.37, -7.9) * mm});
            skLineSegment(sketch, "E1122", {"start": v(19.37, -7.9) * mm, "end": v(19.49, -7.91) * mm});
            skLineSegment(sketch, "E1123", {"start": v(19.49, -7.91) * mm, "end": v(19.61, -7.93) * mm});
            skLineSegment(sketch, "E1124", {"start": v(19.61, -7.93) * mm, "end": v(19.75, -7.94) * mm});
            skLineSegment(sketch, "E1125", {"start": v(19.75, -7.94) * mm, "end": v(19.9, -7.95) * mm});
            skLineSegment(sketch, "E1126", {"start": v(19.9, -7.95) * mm, "end": v(20.06, -7.95) * mm});
            skLineSegment(sketch, "E1127", {"start": v(20.06, -7.95) * mm, "end": v(20.22, -7.95) * mm});
            skLineSegment(sketch, "E1128", {"start": v(20.22, -7.95) * mm, "end": v(20.4, -7.95) * mm});
            skLineSegment(sketch, "E1129", {"start": v(20.4, -7.95) * mm, "end": v(20.59, -7.95) * mm});
            skLineSegment(sketch, "E1130", {"start": v(20.59, -7.95) * mm, "end": v(20.78, -7.94) * mm});
            skLineSegment(sketch, "E1131", {"start": v(20.78, -7.94) * mm, "end": v(20.99, -7.92) * mm});
            skLineSegment(sketch, "E1132", {"start": v(20.99, -7.92) * mm, "end": v(21.2, -7.9) * mm});
            skLineSegment(sketch, "E1133", {"start": v(21.2, -7.9) * mm, "end": v(21.42, -7.88) * mm});
            skLineSegment(sketch, "E1134", {"start": v(21.42, -7.88) * mm, "end": v(21.66, -7.85) * mm});
            skLineSegment(sketch, "E1135", {"start": v(21.66, -7.85) * mm, "end": v(21.9, -7.8) * mm});
            skLineSegment(sketch, "E1136", {"start": v(21.9, -7.8) * mm, "end": v(22.15, -7.76) * mm});
            skLineSegment(sketch, "E1137", {"start": v(22.15, -7.76) * mm, "end": v(22.4, -7.7) * mm});
            skLineSegment(sketch, "E1138", {"start": v(22.4, -7.7) * mm, "end": v(22.67, -7.65) * mm});
            skLineSegment(sketch, "E1139", {"start": v(22.67, -7.65) * mm, "end": v(22.94, -7.58) * mm});
            skLineSegment(sketch, "E1140", {"start": v(22.94, -7.58) * mm, "end": v(23.22, -7.5) * mm});
            skLineSegment(sketch, "E1141", {"start": v(23.22, -7.5) * mm, "end": v(23.51, -7.41) * mm});
            skLineSegment(sketch, "E1142", {"start": v(23.51, -7.41) * mm, "end": v(23.81, -7.32) * mm});
            skLineSegment(sketch, "E1143", {"start": v(23.81, -7.32) * mm, "end": v(24.11, -7.21) * mm});
            skLineSegment(sketch, "E1144", {"start": v(24.11, -7.21) * mm, "end": v(24.42, -7.1) * mm});
            skLineSegment(sketch, "E1145", {"start": v(24.42, -7.1) * mm, "end": v(24.62, -6.94) * mm});
            skLineSegment(sketch, "E1146", {"start": v(24.62, -6.94) * mm, "end": v(24.83, -6.15) * mm});
            skLineSegment(sketch, "E1147", {"start": v(24.83, -6.15) * mm, "end": v(24.74, -5.91) * mm});
            skLineSegment(sketch, "E1148", {"start": v(24.74, -5.91) * mm, "end": v(24.53, -5.66) * mm});
            skLineSegment(sketch, "E1149", {"start": v(24.53, -5.66) * mm, "end": v(24.31, -5.42) * mm});
            skLineSegment(sketch, "E1150", {"start": v(24.31, -5.42) * mm, "end": v(24.1, -5.19) * mm});
            skLineSegment(sketch, "E1151", {"start": v(24.1, -5.19) * mm, "end": v(23.9, -4.97) * mm});
            skLineSegment(sketch, "E1152", {"start": v(23.9, -4.97) * mm, "end": v(23.69, -4.76) * mm});
            skLineSegment(sketch, "E1153", {"start": v(23.69, -4.76) * mm, "end": v(23.48, -4.57) * mm});
            skLineSegment(sketch, "E1154", {"start": v(23.48, -4.57) * mm, "end": v(23.28, -4.38) * mm});
            skLineSegment(sketch, "E1155", {"start": v(23.28, -4.38) * mm, "end": v(23.09, -4.2) * mm});
            skLineSegment(sketch, "E1156", {"start": v(23.09, -4.2) * mm, "end": v(22.9, -4.04) * mm});
            skLineSegment(sketch, "E1157", {"start": v(22.9, -4.04) * mm, "end": v(22.7, -3.9) * mm});
            skLineSegment(sketch, "E1158", {"start": v(22.7, -3.9) * mm, "end": v(22.52, -3.75) * mm});
            skLineSegment(sketch, "E1159", {"start": v(22.52, -3.75) * mm, "end": v(22.33, -3.62) * mm});
            skLineSegment(sketch, "E1160", {"start": v(22.33, -3.62) * mm, "end": v(22.16, -3.5) * mm});
            skLineSegment(sketch, "E1161", {"start": v(22.16, -3.5) * mm, "end": v(21.99, -3.38) * mm});
            skLineSegment(sketch, "E1162", {"start": v(21.99, -3.38) * mm, "end": v(21.82, -3.27) * mm});
            skLineSegment(sketch, "E1163", {"start": v(21.82, -3.27) * mm, "end": v(21.66, -3.18) * mm});
            skLineSegment(sketch, "E1164", {"start": v(21.66, -3.18) * mm, "end": v(21.51, -3.09) * mm});
            skLineSegment(sketch, "E1165", {"start": v(21.51, -3.09) * mm, "end": v(21.36, -3) * mm});
            skLineSegment(sketch, "E1166", {"start": v(21.36, -3) * mm, "end": v(21.23, -2.94) * mm});
            skLineSegment(sketch, "E1167", {"start": v(21.23, -2.94) * mm, "end": v(21.1, -2.87) * mm});
            skLineSegment(sketch, "E1168", {"start": v(21.1, -2.87) * mm, "end": v(20.97, -2.81) * mm});
            skLineSegment(sketch, "E1169", {"start": v(20.97, -2.81) * mm, "end": v(20.85, -2.76) * mm});
            skLineSegment(sketch, "E1170", {"start": v(20.85, -2.76) * mm, "end": v(20.74, -2.71) * mm});
            skLineSegment(sketch, "E1171", {"start": v(20.74, -2.71) * mm, "end": v(20.64, -2.67) * mm});
            skLineSegment(sketch, "E1172", {"start": v(20.64, -2.67) * mm, "end": v(20.55, -2.64) * mm});
            skLineSegment(sketch, "E1173", {"start": v(20.55, -2.64) * mm, "end": v(20.46, -2.61) * mm});
            skLineSegment(sketch, "E1174", {"start": v(20.46, -2.61) * mm, "end": v(20.39, -2.59) * mm});
            skLineSegment(sketch, "E1175", {"start": v(20.39, -2.59) * mm, "end": v(20.32, -2.57) * mm});
            skLineSegment(sketch, "E1176", {"start": v(20.32, -2.57) * mm, "end": v(20.26, -2.55) * mm});
            skLineSegment(sketch, "E1177", {"start": v(20.26, -2.55) * mm, "end": v(20.2, -2.54) * mm});
            skLineSegment(sketch, "E1178", {"start": v(20.2, -2.54) * mm, "end": v(20.17, -2.53) * mm});
            skLineSegment(sketch, "E1179", {"start": v(20.17, -2.53) * mm, "end": v(20.14, -2.53) * mm});
            skLineSegment(sketch, "E1180", {"start": v(20.14, -2.53) * mm, "end": v(20.12, -2.52) * mm});
            skLineSegment(sketch, "E1181", {"start": v(20.12, -2.52) * mm, "end": v(20.1, -2.52) * mm});
            skLineSegment(sketch, "E1182", {"start": v(20.1, -2.52) * mm, "end": v(19.32, -2.42) * mm});
            skLineSegment(sketch, "E1183", {"start": v(19.32, -2.42) * mm, "end": v(19.47, 0) * mm});
            skSolve(sketch);
        }
        {
            var Q0;
            Q0=qSketchRegion(id+"F0",true);
            extrude(context, id + "F1", {"entities" : qUnion([Q0]), "depth" : 25.4 * mm});
        }
    });
